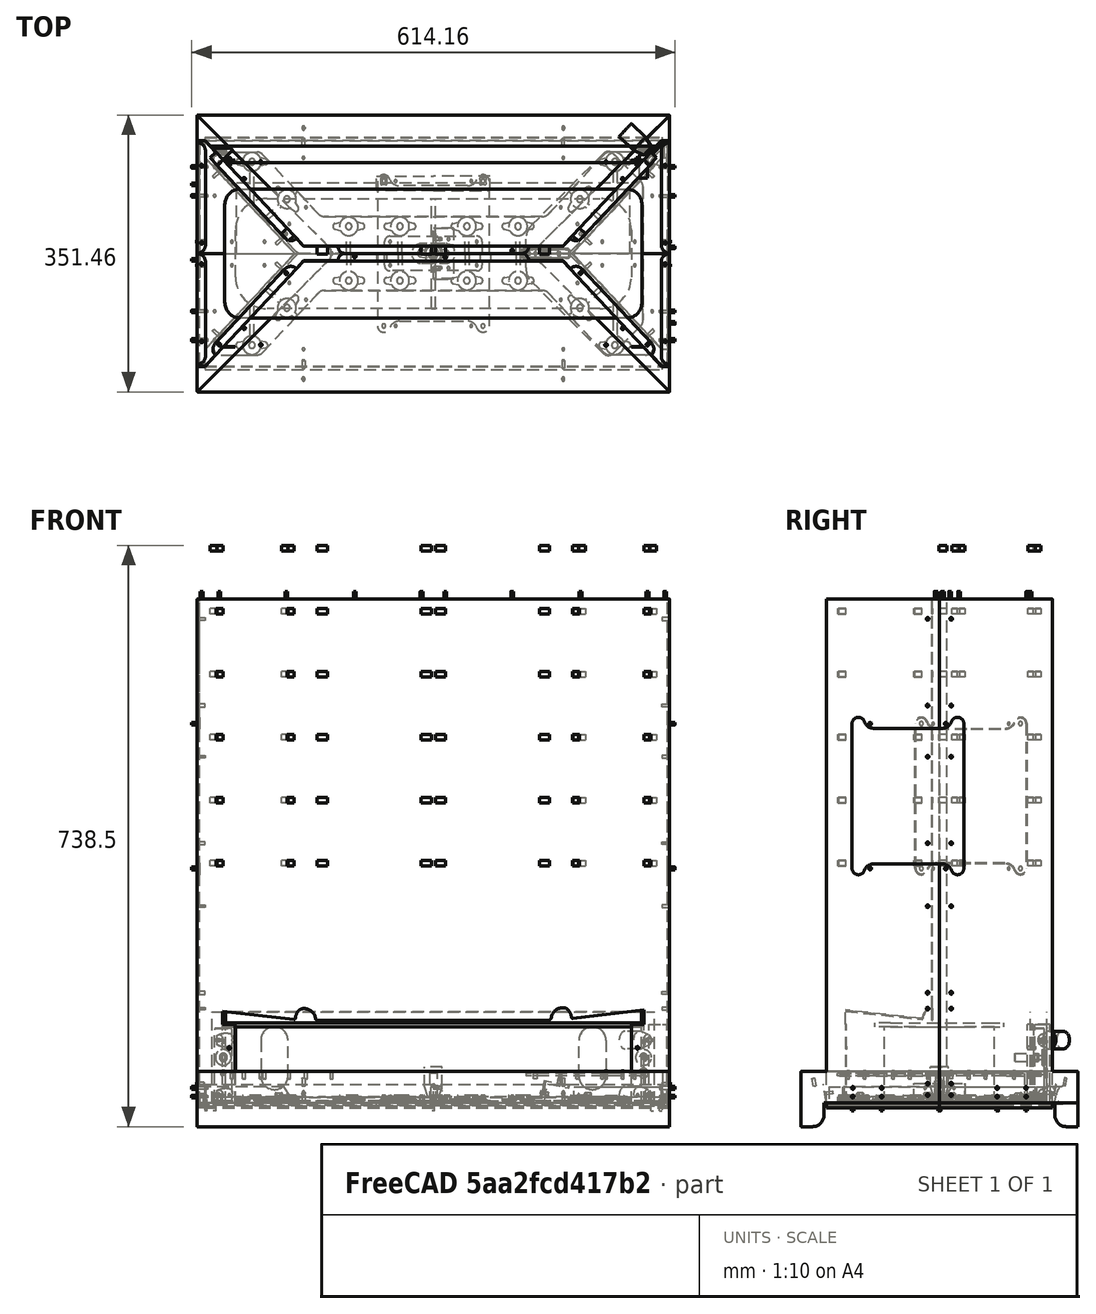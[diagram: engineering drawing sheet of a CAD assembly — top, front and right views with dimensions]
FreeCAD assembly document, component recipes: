
FREECAD ASSEMBLY — COMPONENT RECIPES ("composit_stand6")

This assembly document has 25 components, labeled P0..P24 below (a component is one placed body or linked part). 24 of them carry a construction recipe — the FreeCAD feature program that regenerates the part from scratch, quoted from this document or its linked companion documents; the rest are supplied as boundary geometry only. No exploded tour is included for this assembly.
COMPONENT P0 — recipe-attached ("basin", modeled in this document).
Construction recipe (the document's own serialized feature program — sketch geometry with constraints, then the solid features built on it; lengths are millimeters unless a unit is written):

FEATURE [Sketcher::SketchObject] Sketch015
  AttachmentOffset = pos=(0,0,97) rot=(0,0,1;0rad)
  FullyConstrained = true
  MapMode = 5
  Placement = pos=(0,0,97) rot=(0,0,1;0rad)
  Support = -> [XY_Plane006]
  expr: .AttachmentOffset.Base.z = Pad001.Length
  sketch-geometry (10):
    g0: ArcOfCircle CenterX=-245 CenterY=-62 CenterZ=0 NormalX=0 NormalY=0 NormalZ=1 AngleXU=0 Radius=20 StartAngle=3.14159 EndAngle=4.71239
    g1: LineSegment StartX=-265 StartY=-62 StartZ=0 EndX=-265 EndY=62 EndZ=0
    g2: ArcOfCircle CenterX=-245 CenterY=62 CenterZ=0 NormalX=0 NormalY=0 NormalZ=1 AngleXU=0 Radius=20 StartAngle=1.5708 EndAngle=3.14159
    g3: LineSegment StartX=-245 StartY=82 StartZ=0 EndX=245 EndY=82 EndZ=0
    g4: ArcOfCircle CenterX=245 CenterY=62 CenterZ=0 NormalX=0 NormalY=0 NormalZ=1 AngleXU=0 Radius=20 StartAngle=8.58e-14 EndAngle=1.5708
    g5: LineSegment StartX=265 StartY=62 StartZ=0 EndX=265 EndY=-62 EndZ=0
    g6: ArcOfCircle CenterX=245 CenterY=-62 CenterZ=0 NormalX=0 NormalY=0 NormalZ=1 AngleXU=0 Radius=20 StartAngle=4.71239 EndAngle=6.28319
    g7: LineSegment StartX=245 StartY=-82 StartZ=0 EndX=-245 EndY=-82 EndZ=0
    g8: GeomPoint X=-265 Y=-82 Z=0
    g9: GeomPoint X=265 Y=82 Z=0
  constraints (23):
    c: Tangent(g0,g1) = 1.5708
    c: Tangent(g1,g2) = 1.5708
    c: Tangent(g2,g3) = 1.5708
    c: Tangent(g3,g4) = 1.5708
    c: Tangent(g4,g5) = 1.5708
    c: Tangent(g5,g6) = 1.5708
    c: Tangent(g6,g7) = 1.5708
    c: Tangent(g7,g0) = 1.5708
    c: Horizontal(g3)
    c: Horizontal(g7)
    c: Vertical(g1)
    c: Vertical(g5)
    c: Equal(g0,g2)
    c: Equal(g2,g4)
    c: Equal(g4,g6)
    c: PointOnObject(g8,g1)
    c: PointOnObject(g8,g7)
    c: PointOnObject(g9,g3)
    c: PointOnObject(g9,g5)
    c: Symmetric(g8,g9,g-1)
    c: DistanceX(g8,g9) = 530
    c: DistanceY(g8,g9) = 164
    c: Radius(g4) = 20
FEATURE [Sketcher::SketchObject] Sketch016
  FullyConstrained = true
  MapMode = 5
  Support = -> [XY_Plane006]
  sketch-geometry (10):
    g0: ArcOfCircle CenterX=-211.5 CenterY=-30 CenterZ=0 NormalX=0 NormalY=0 NormalZ=1 AngleXU=0 Radius=40 StartAngle=3.14159 EndAngle=4.71239
    g1: LineSegment StartX=-251.5 StartY=-30 StartZ=0 EndX=-251.5 EndY=30 EndZ=0
    g2: ArcOfCircle CenterX=-211.5 CenterY=30 CenterZ=0 NormalX=0 NormalY=0 NormalZ=1 AngleXU=0 Radius=40 StartAngle=1.5708 EndAngle=3.14159
    g3: LineSegment StartX=-211.5 StartY=70 StartZ=0 EndX=211.5 EndY=70 EndZ=0
    g4: ArcOfCircle CenterX=211.5 CenterY=30 CenterZ=0 NormalX=0 NormalY=0 NormalZ=1 AngleXU=0 Radius=40 StartAngle=6.3434e-12 EndAngle=1.5708
    g5: LineSegment StartX=251.5 StartY=30 StartZ=0 EndX=251.5 EndY=-30 EndZ=0
    g6: ArcOfCircle CenterX=211.5 CenterY=-30 CenterZ=0 NormalX=0 NormalY=0 NormalZ=1 AngleXU=0 Radius=40 StartAngle=4.71239 EndAngle=6.28319
    g7: LineSegment StartX=211.5 StartY=-70 StartZ=0 EndX=-211.5 EndY=-70 EndZ=0
    g8: GeomPoint X=-251.5 Y=-70 Z=0
    g9: GeomPoint X=251.5 Y=70 Z=0
  constraints (23):
    c: Tangent(g0,g1) = 1.5708
    c: Tangent(g1,g2) = 1.5708
    c: Tangent(g2,g3) = 1.5708
    c: Tangent(g3,g4) = 1.5708
    c: Tangent(g4,g5) = 1.5708
    c: Tangent(g5,g6) = 1.5708
    c: Tangent(g6,g7) = 1.5708
    c: Tangent(g7,g0) = 1.5708
    c: Horizontal(g3)
    c: Horizontal(g7)
    c: Vertical(g1)
    c: Vertical(g5)
    c: Equal(g0,g2)
    c: Equal(g2,g4)
    c: Equal(g4,g6)
    c: PointOnObject(g8,g1)
    c: PointOnObject(g8,g7)
    c: PointOnObject(g9,g3)
    c: PointOnObject(g9,g5)
    c: Symmetric(g8,g9,g-1)
    c: Radius(g4) = 40
    c: DistanceX(g8,g9) = 503
    c: DistanceY(g8,g9) = 140
FEATURE [PartDesign::Pad] Pad001
  Direction = (0,0,1)
  Length = 97
  Length2 = 10
  Profile = -> Sketch016
  ReferenceAxis = -> Sketch016 [N_Axis]
  Type = 0
FEATURE [PartDesign::Pad] Pad002
  BaseFeature = -> Pad001
  Direction = (0,0,1)
  Length = 5
  Length2 = 10
  Profile = -> Sketch015
  ReferenceAxis = -> Sketch015 [N_Axis]
  Type = 0
FEATURE [PartDesign::Body] Body005  label="basin"
  Group = -> [Sketch015,Sketch016,Pad001,Pad002]
  Origin = -> Origin006
  Tip = -> Pad002
COMPONENT P1 — recipe-attached ("face2_material_0.30ansi", modeled in this document).
Construction recipe (the document's own serialized feature program — sketch geometry with constraints, then the solid features built on it; lengths are millimeters unless a unit is written):

FEATURE [PartDesign::FeatureBase] BaseFeature
  BaseFeature = -> Boolean
  expr: BaseFeature = <<face2_origin>>._self
FEATURE [PartDesign::Boolean] Boolean001
  BaseFeature = -> BaseFeature
  Group = -> [Compound009]
  Type = 1
FEATURE [PartDesign::Boolean] Boolean017
  BaseFeature = -> Boolean001
  Group = -> [Compound025]
  Type = 0
FEATURE [PartDesign::Body] Body007  label="face2_material_0.30ansi"
  BaseFeature = -> Boolean
  Group = -> [BaseFeature,Boolean001,Boolean017]
  Origin = -> Origin008
  Placement = pos=(0,0,0) rot=(0,0,1;3.14159rad)
  Tip = -> Boolean017
COMPONENT P2 — recipe-attached ("electric_shield", modeled in this document).
Construction recipe (the document's own serialized feature program — sketch geometry with constraints, then the solid features built on it; lengths are millimeters unless a unit is written):

FEATURE [PartDesign::SubShapeBinder] Binder045
  BindCopyOnChange = 0
  BindMode = 0
  ClaimChildren = true
  Context = -> Body008 [Binder045.]
  Fuse = false
  MakeFace = true
  OffsetFill = false
  OffsetIntersection = false
  OffsetJoinType = 0
  OffsetOpenResult = false
  PartialLoad = false
  Relative = false
  Support = -> [Connect005]
  _Version = 2
  expr: Support = <<Connect005>>._self
FEATURE [PartDesign::Pad] Pad015
  Direction = (0,0,1)
  Length = 0.3
  Length2 = 10
  Profile = -> Binder045
  Type = 0
FEATURE [PartDesign::Boolean] Boolean002
  BaseFeature = -> Pad015
  Group = -> [Compound010]
  Type = 1
FEATURE [PartDesign::Body] Body008  label="electric_shield"
  Group = -> [Binder045,Pad015,Boolean002]
  Origin = -> Origin009
  Placement = pos=(-297.084,40,390) rot=(0.57735,-0.57735,-0.57735;2.0944rad)
  Tip = -> Boolean002
  expr: Placement = <<electric_shield_placement>>.Placement
COMPONENT P3 — recipe-attached ("lamp_fix", modeled in this document).
Construction recipe (the document's own serialized feature program — sketch geometry with constraints, then the solid features built on it; lengths are millimeters unless a unit is written):

FEATURE [PartDesign::SubShapeBinder] Binder022
  BindCopyOnChange = 0
  BindMode = 0
  ClaimChildren = true
  Context = -> Body012 [Binder022.]
  Fuse = false
  MakeFace = true
  OffsetFill = false
  OffsetIntersection = false
  OffsetJoinType = 0
  OffsetOpenResult = false
  PartialLoad = false
  Placement = pos=(0,0,0) rot=(1,0,0;1.5708rad)
  Relative = false
  Support = -> [Sketch031]
  _Version = 2
FEATURE [PartDesign::Pad] Pad007
  Direction = (0,-1,2e-16)
  Length = 10
  Length2 = 10
  Midplane = true
  Placement = pos=(0,0,0) rot=(1,0,0;1.5708rad)
  Profile = -> Binder022
  Type = 0
FEATURE [PartDesign::Boolean] Boolean009
  BaseFeature = -> Pad007
  Group = -> [Compound018]
  Type = 1
FEATURE [PartDesign::Body] Body012  label="lamp_fix"
  Group = -> [Binder022,Pad007,Boolean009]
  Origin = -> Origin014
  Tip = -> Boolean009
COMPONENT P4 — recipe-attached ("faces_connect", modeled in this document).
Construction recipe (the document's own serialized feature program — sketch geometry with constraints, then the solid features built on it; lengths are millimeters unless a unit is written):

FEATURE [PartDesign::SubShapeBinder] Binder023
  BindCopyOnChange = 0
  BindMode = 0
  ClaimChildren = true
  Context = -> Body013 [Binder023.]
  Fuse = false
  MakeFace = true
  OffsetFill = false
  OffsetIntersection = false
  OffsetJoinType = 0
  OffsetOpenResult = false
  PartialLoad = false
  Relative = false
  Support = -> [Sketch032]
  _Version = 2
FEATURE [PartDesign::Pad] Pad008
  Direction = (0,0,1)
  Length = 3
  Length2 = 10
  Profile = -> Binder023
  Type = 0
FEATURE [PartDesign::Boolean] Boolean010
  BaseFeature = -> Pad008
  Group = -> [Populate027]
  Type = 1
FEATURE [PartDesign::Body] Body013  label="faces_connect"
  Group = -> [Binder023,Pad008,Boolean010]
  Origin = -> Origin015
  Tip = -> Boolean010
COMPONENT P5 — recipe-attached ("electric_shield_jamb", modeled in this document).
Construction recipe (the document's own serialized feature program — sketch geometry with constraints, then the solid features built on it; lengths are millimeters unless a unit is written):

FEATURE [PartDesign::SubShapeBinder] Binder025
  BindCopyOnChange = 0
  BindMode = 0
  ClaimChildren = true
  Context = -> Body015 [Binder025.]
  Fuse = false
  MakeFace = true
  OffsetFill = false
  OffsetIntersection = false
  OffsetJoinType = 0
  OffsetOpenResult = false
  PartialLoad = false
  Relative = false
  Support = -> [Compound021]
  _Version = 2
FEATURE [PartDesign::Pad] Pad009
  Direction = (0,0,1)
  Length = 3
  Length2 = 10
  Profile = -> Binder025
  Type = 0
FEATURE [PartDesign::Boolean] Boolean013
  BaseFeature = -> Pad009
  Group = -> [Fusion003]
  Type = 1
FEATURE [PartDesign::Body] Body015  label="electric_shield_jamb"
  Group = -> [Binder025,Pad009,Boolean013]
  Origin = -> Origin017
  Tip = -> Boolean013
COMPONENT P6 — recipe-attached ("screw_pocket", modeled in this document).
Construction recipe (the document's own serialized feature program — sketch geometry with constraints, then the solid features built on it; lengths are millimeters unless a unit is written):

FEATURE [Sketcher::SketchObject] Sketch040
  FullyConstrained = true
  MapMode = 5
  Support = -> [XY_Plane018]
  sketch-geometry (7):
    g0: ArcOfCircle CenterX=2.79363 CenterY=2.79363 CenterZ=0 NormalX=0 NormalY=0 NormalZ=1 AngleXU=0 Radius=1.6 StartAngle=5.49779 EndAngle=8.63938
    g1: LineSegment StartX=3.925 StartY=3.925 StartZ=0 EndX=1.66226 EndY=3.925 EndZ=0
    g2: LineSegment StartX=1.66226 StartY=3.925 StartZ=0 EndX=0 EndY=3.925 EndZ=0
    g3: LineSegment StartX=3.925 StartY=0 StartZ=0 EndX=3.925 EndY=1.66226 EndZ=0
    g4: LineSegment StartX=3.925 StartY=1.66226 StartZ=0 EndX=3.925 EndY=3.925 EndZ=0
    g5: LineSegment StartX=0 StartY=3.925 StartZ=0 EndX=0 EndY=0 EndZ=0
    g6: LineSegment StartX=0 StartY=0 StartZ=0 EndX=3.925 EndY=0 EndZ=0
  constraints (20):
    c: PointOnObject(g3,g-1)
    c: Coincident(g4,g1)
    c: PointOnObject(g2,g-2)
    c: Coincident(g1,g2)
    c: Horizontal(g1)
    c: Horizontal(g2)
    c: Coincident(g3,g4)
    c: Vertical(g3)
    c: Vertical(g4)
    c: Coincident(g2,g0)
    c: Coincident(g3,g0)
    c: Coincident(g2,g5)
    c: Coincident(g5,g-1)
    c: Coincident(g5,g6)
    c: Coincident(g6,g3)
    c: Equal(g6,g5)
    c: DistanceX(g6,g6) = 3.925
    c: PointOnObject(g1,g0)
    c: Equal(g4,g1)
    c: Diameter(g0) = 3.2
FEATURE [PartDesign::Pad] Pad010
  Direction = (0,0,1)
  Length = 3
  Length2 = 10
  Midplane = true
  Profile = -> Sketch040
  ReferenceAxis = -> Sketch040 [N_Axis]
  Type = 0
FEATURE [PartDesign::PolarPattern] PolarPattern001
  Angle = 360
  Axis = -> Sketch040 [N_Axis]
  BaseFeature = -> Pad010
  Mode = 0
  Occurrences = 4
  Offset = 120
  Originals = -> [Pad010]
  Refine = true
FEATURE [PartDesign::Body] Body016  label="screw_pocket"
  Group = -> [Sketch040,Pad010,PolarPattern001]
  Origin = -> Origin018
  Tip = -> PolarPattern001
COMPONENT P7 — recipe-attached ("front_shield_jamb", modeled in this document).
Construction recipe (the document's own serialized feature program — sketch geometry with constraints, then the solid features built on it; lengths are millimeters unless a unit is written):

FEATURE [PartDesign::SubShapeBinder] Binder030
  BindCopyOnChange = 0
  BindMode = 0
  ClaimChildren = false
  Context = -> Body018 [Binder030.]
  Fuse = false
  MakeFace = true
  OffsetFill = false
  OffsetIntersection = false
  OffsetJoinType = 0
  OffsetOpenResult = false
  PartialLoad = false
  Relative = true
  Support = -> [Sketch001]
  _Version = 2
FEATURE [PartDesign::CoordinateSystem] Local_CS001
  AttacherType = Attacher::AttachEngine3D
  MapMode = 1
  Placement = pos=(266.917,133.558,0) rot=(0,0.707107,0.707107;3.14159rad)
FEATURE [PartDesign::SubShapeBinder] Binder039
  BindCopyOnChange = 0
  BindMode = 0
  ClaimChildren = true
  Context = -> Body018 [Binder039.]
  Fuse = false
  MakeFace = true
  OffsetFill = false
  OffsetIntersection = false
  OffsetJoinType = 0
  OffsetOpenResult = false
  PartialLoad = false
  Relative = false
  Support = -> [Sketch056]
  _Version = 2
FEATURE [PartDesign::Pad] Pad011
  Direction = (0,0,1)
  Length = 95
  Length2 = 10
  Profile = -> Binder039
  Type = 0
FEATURE [PartDesign::Fillet] Fillet
  Base = -> Pad011
  BaseFeature = -> Pad011
  Radius = 2
  SupportTransform = false
  UseAllEdges = true
FEATURE [PartDesign::Boolean] Boolean016
  BaseFeature = -> Fillet
  Group = -> [Fusion004]
  Type = 1
FEATURE [PartDesign::Body] Body018  label="front_shield_jamb"
  Group = -> [Binder030,Pad011,Local_CS001,Binder039,Fillet,Boolean016]
  Origin = -> Origin025
  Tip = -> Boolean016
COMPONENT P8 — recipe-attached ("Body019", modeled in this document).
Construction recipe (the document's own serialized feature program — sketch geometry with constraints, then the solid features built on it; lengths are millimeters unless a unit is written):

FEATURE [PartDesign::SubShapeBinder] Binder032
  BindCopyOnChange = 0
  BindMode = 0
  ClaimChildren = true
  Context = -> Body019 [Binder032.]
  Fuse = false
  MakeFace = true
  OffsetFill = false
  OffsetIntersection = false
  OffsetJoinType = 0
  OffsetOpenResult = false
  PartialLoad = false
  Relative = false
  Support = -> [Connect002]
  _Version = 2
FEATURE [PartDesign::FeaturePython] BaseBend006  # WARN: FeaturePython — macro-defined, semantics opaque (R4)
  BendSide = 1
  BendSketch = -> Binder032
  MidPlane = false
  Reverse = false
  length = 116
  radius = 0.1
  thickness = 0.3
FEATURE [PartDesign::Boolean] Boolean020
  BaseFeature = -> BaseBend006
  Group = -> [Compound028]
  Refine = true
  Type = 1
FEATURE [PartDesign::Body] Body019
  Group = -> [Binder032,BaseBend006,Boolean020]
  Origin = -> Origin026
  Tip = -> Boolean020
COMPONENT P9 — recipe-attached ("Body020", modeled in this document).
Construction recipe (the document's own serialized feature program — sketch geometry with constraints, then the solid features built on it; lengths are millimeters unless a unit is written):

FEATURE [PartDesign::SubShapeBinder] Binder033
  BindCopyOnChange = 0
  BindMode = 0
  ClaimChildren = true
  Context = -> Body020 [Binder033.]
  Fuse = false
  MakeFace = true
  OffsetFill = false
  OffsetIntersection = false
  OffsetJoinType = 0
  OffsetOpenResult = false
  PartialLoad = false
  Relative = false
  Support = -> [Sketch051]
  _Version = 2
FEATURE [PartDesign::FeaturePython] BaseBend007  # WARN: FeaturePython — macro-defined, semantics opaque (R4)
  BendSide = 0
  BendSketch = -> Binder033
  MidPlane = false
  Reverse = false
  length = 100
  radius = 0.1
  thickness = 0.3
FEATURE [PartDesign::Boolean] Boolean018
  BaseFeature = -> BaseBend007
  Group = -> [Compound026]
  Type = 1
FEATURE [PartDesign::Body] Body020
  Group = -> [Binder033,BaseBend007,Boolean018]
  Origin = -> Origin027
  Tip = -> Boolean018
COMPONENT P10 — recipe-attached ("Body021", modeled in this document).
Construction recipe (the document's own serialized feature program — sketch geometry with constraints, then the solid features built on it; lengths are millimeters unless a unit is written):

FEATURE [PartDesign::SubShapeBinder] Binder034
  BindCopyOnChange = 0
  BindMode = 0
  ClaimChildren = true
  Context = -> Body021 [Binder034.]
  Fuse = false
  MakeFace = true
  OffsetFill = false
  OffsetIntersection = false
  OffsetJoinType = 0
  OffsetOpenResult = false
  PartialLoad = false
  Relative = false
  Support = -> [Part__Mirroring009]
  _Version = 2
FEATURE [PartDesign::FeaturePython] BaseBend008  # WARN: FeaturePython — macro-defined, semantics opaque (R4)
  BendSide = 1
  BendSketch = -> Binder034
  MidPlane = false
  Reverse = false
  length = 100
  radius = 0.1
  thickness = 0.3
FEATURE [PartDesign::Boolean] Boolean019
  BaseFeature = -> BaseBend008
  Group = -> [Compound027]
  Type = 1
FEATURE [PartDesign::Body] Body021
  Group = -> [Binder034,BaseBend008,Boolean019]
  Origin = -> Origin028
  Tip = -> Boolean019
COMPONENT P11 — recipe-attached ("Body022", modeled in this document).
Construction recipe (the document's own serialized feature program — sketch geometry with constraints, then the solid features built on it; lengths are millimeters unless a unit is written):

FEATURE [PartDesign::SubShapeBinder] Binder035
  BindCopyOnChange = 0
  BindMode = 0
  ClaimChildren = true
  Context = -> Part002 [Part004.Body017.Boolean015.Body022.Binder035.]
  Fuse = false
  MakeFace = true
  OffsetFill = false
  OffsetIntersection = false
  OffsetJoinType = 0
  OffsetOpenResult = false
  PartialLoad = false
  Relative = true
  Support = -> [Compound023]
  _Version = 2
  expr: Support = <<Compound023>>._self
FEATURE [PartDesign::FeaturePython] BaseBend009  # WARN: FeaturePython — macro-defined, semantics opaque (R4)
  BendSide = 0
  BendSketch = -> Binder035
  MidPlane = false
  Reverse = true
  length = 30
  radius = 0.1
  thickness = 0.3
FEATURE [Sketcher::SketchObject] Sketch052
  ExternalGeometry = -> [Binder035]
  FullyConstrained = true
  MapMode = 5
  Placement = pos=(0,0,0) rot=(0.57735,0.57735,0.57735;2.0944rad)
  Support = -> [YZ_Plane029]
  sketch-geometry (3):
    g0: ArcOfCircle CenterX=161.558 CenterY=-15 CenterZ=0 NormalX=0 NormalY=0 NormalZ=1 AngleXU=0 Radius=15 StartAngle=3.14159 EndAngle=4.71239
    g1: LineSegment StartX=146.558 StartY=-15 StartZ=0 EndX=146.558 EndY=-30 EndZ=0
    g2: LineSegment StartX=146.558 StartY=-30 StartZ=0 EndX=161.558 EndY=-30 EndZ=0
  constraints (9):
    c: Coincident(g1,g2)
    c: Coincident(g2,g0)
    c: Tangent(g2,g0)
    c: Tangent(g0,g1) = -1.5708
    c: Horizontal(g2)
    c: Vertical(g1)
    c: Vertical(g1,g-3)
    c: DistanceY(g1,g-3) = 30
    c: Diameter(g0) = 30
FEATURE [PartDesign::Pocket] Pocket012
  BaseFeature = -> BaseBend009
  Direction = (-1,0,0)
  Length = 5
  Length2 = 5
  Midplane = true
  Profile = -> Sketch052
  ReferenceAxis = -> Sketch052 [N_Axis]
  Type = 1
FEATURE [PartDesign::Body] Body022
  Group = -> [Binder035,BaseBend009,Sketch052,Pocket012]
  Origin = -> Origin029
  Tip = -> Pocket012
COMPONENT P12 — recipe-attached ("Body024", modeled in this document).
Construction recipe (the document's own serialized feature program — sketch geometry with constraints, then the solid features built on it; lengths are millimeters unless a unit is written):

FEATURE [PartDesign::SubShapeBinder] Binder036
  BindCopyOnChange = 0
  BindMode = 0
  ClaimChildren = true
  Context = -> Body024 [Binder036.]
  Fuse = false
  MakeFace = true
  OffsetFill = false
  OffsetIntersection = false
  OffsetJoinType = 0
  OffsetOpenResult = false
  PartialLoad = false
  Relative = false
  Support = -> [Connect003]
  _Version = 2
FEATURE [PartDesign::Pad] Pad012
  Direction = (0,0,1)
  Length = 3
  Length2 = 10
  Profile = -> Binder036
  Refine = true
  Type = 0
FEATURE [PartDesign::Boolean] Boolean021
  BaseFeature = -> Pad012
  Group = -> [Compound031]
  Type = 1
FEATURE [PartDesign::Body] Body024
  Group = -> [Binder036,Pad012,Boolean021]
  Origin = -> Origin031
  Tip = -> Boolean021
COMPONENT P13 — recipe-attached ("Body025", modeled in this document).
Construction recipe (the document's own serialized feature program — sketch geometry with constraints, then the solid features built on it; lengths are millimeters unless a unit is written):

FEATURE [Sketcher::SketchObject] Sketch055
  FullyConstrained = true
  MapMode = 5
  Placement = pos=(0,0,0) rot=(1,0,0;1.5708rad)
  Support = -> [XZ_Plane032]
  sketch-geometry (7):
    g0: LineSegment StartX=0 StartY=0 StartZ=0 EndX=7 EndY=0 EndZ=0
    g1: LineSegment StartX=7 StartY=0 StartZ=0 EndX=11.25 EndY=14 EndZ=0
    g2: LineSegment StartX=11.25 StartY=14 StartZ=0 EndX=0 EndY=14 EndZ=0
    g3: LineSegment StartX=0 StartY=14 StartZ=0 EndX=0 EndY=0 EndZ=0
    g4: LineSegment StartX=11.25 StartY=14 StartZ=0 EndX=11.25 EndY=39 EndZ=0
    g5: LineSegment StartX=11.25 StartY=39 StartZ=0 EndX=0 EndY=39 EndZ=0
    g6: LineSegment StartX=0 StartY=39 StartZ=0 EndX=0 EndY=14 EndZ=0
  constraints (19):
    c: Horizontal(g0)
    c: Coincident(g0,g1)
    c: Coincident(g1,g2)
    c: Horizontal(g2)
    c: Coincident(g2,g3)
    c: Coincident(g3,g0)
    c: Vertical(g3)
    c: Coincident(g0,g-1)
    c: DistanceX(g2,g2) = 11.25
    c: DistanceX(g0,g0) = 7
    c: DistanceY(g3,g3) = 14
    c: Coincident(g1,g4)
    c: Vertical(g4)
    c: Coincident(g4,g5)
    c: Horizontal(g5)
    c: Coincident(g5,g6)
    c: Coincident(g6,g3)
    c: Vertical(g6)
    c: DistanceY(g6,g6) = 25
FEATURE [PartDesign::Revolution] Revolution
  Angle = 360
  Axis = (0,2e-16,1)
  Base = (0,0,0)
  Placement = pos=(0,0,0) rot=(1,0,0;1.5708rad)
  Profile = -> Sketch055
  ReferenceAxis = -> Sketch055 [V_Axis]
  Reversed = true
FEATURE [PartDesign::Body] Body025
  Group = -> [Sketch055,Revolution]
  Origin = -> Origin032
  Placement = pos=(0,0,7) rot=(0,0,1;0rad)
  Tip = -> Revolution
COMPONENT P14 — recipe-attached ("magnet", modeled in this document).
Construction recipe (the document's own serialized feature program — sketch geometry with constraints, then the solid features built on it; lengths are millimeters unless a unit is written):

FEATURE [Sketcher::SketchObject] Sketch057
  FullyConstrained = true
  MapMode = 5
  Support = -> [XY_Plane033]
  sketch-geometry (1):
    g0: Circle CenterX=0 CenterY=0 CenterZ=0 NormalX=0 NormalY=0 NormalZ=1 AngleXU=0 Radius=10
  constraints (2):
    c: Coincident(g0,g-1)
    c: Diameter(g0) = 20
FEATURE [PartDesign::Pad] Pad013  label="magnet_pad"
  Direction = (0,0,1)
  Length = 3
  Length2 = 10
  Profile = -> Sketch057
  ReferenceAxis = -> Sketch057 [N_Axis]
  Type = 0
FEATURE [PartDesign::Body] Body026  label="magnet"
  Group = -> [Sketch057,Pad013]
  Origin = -> Origin033
  Tip = -> Pad013
COMPONENT P15 — recipe-attached ("front_shield", modeled in this document).
Construction recipe (the document's own serialized feature program — sketch geometry with constraints, then the solid features built on it; lengths are millimeters unless a unit is written):

FEATURE [PartDesign::SubShapeBinder] Binder040
  BindCopyOnChange = 0
  BindMode = 0
  ClaimChildren = true
  Context = -> Body027 [Binder040.]
  Fuse = false
  MakeFace = true
  OffsetFill = false
  OffsetIntersection = false
  OffsetJoinType = 0
  OffsetOpenResult = false
  PartialLoad = false
  Relative = false
  Support = -> [Connect004]
  _Version = 2
FEATURE [PartDesign::FeaturePython] BaseBend010  # WARN: FeaturePython — macro-defined, semantics opaque (R4)
  BendSide = 0
  BendSketch = -> Binder040
  MidPlane = false
  Reverse = false
  length = 116
  radius = 0.1
  thickness = 0.3
FEATURE [PartDesign::SubShapeBinder] Binder041
  BindCopyOnChange = 0
  BindMode = 0
  ClaimChildren = false
  Context = -> Body027 [Binder041.]
  Fuse = false
  MakeFace = true
  OffsetFill = false
  OffsetIntersection = false
  OffsetJoinType = 0
  OffsetOpenResult = false
  PartialLoad = false
  Placement = pos=(202,0,57) rot=(0.57735,0.57735,-0.57735;2.0944rad)
  Relative = true
  Support = -> [<external embedded_hand_34x80.FCStd>#Cut]
  _Version = 2
FEATURE [PartDesign::Pocket] Pocket013
  BaseFeature = -> BaseBend010
  Direction = (0,1,0)
  Length = 5
  Length2 = 5
  Profile = -> Binder041
  Type = 1
FEATURE [PartDesign::Mirrored] Mirrored010
  BaseFeature = -> Pocket013
  MirrorPlane = -> YZ_Plane034
  Originals = -> [Pocket013]
FEATURE [PartDesign::Boolean] Boolean022
  BaseFeature = -> Mirrored010
  Group = -> [Compound032]
  Refine = true
  Type = 1
FEATURE [PartDesign::Body] Body027  label="front_shield"
  Group = -> [Binder040,BaseBend010,Binder041,Pocket013,Mirrored010,Boolean022]
  Origin = -> Origin034
  Tip = -> Boolean022
COMPONENT P16 — recipe-attached ("lamp_holder", modeled in this document).
Construction recipe (the document's own serialized feature program — sketch geometry with constraints, then the solid features built on it; lengths are millimeters unless a unit is written):

FEATURE [PartDesign::SubShapeBinder] Binder042
  BindCopyOnChange = 0
  BindMode = 0
  ClaimChildren = true
  Context = -> Part [Body028.Binder042.]
  Fuse = false
  MakeFace = true
  OffsetFill = false
  OffsetIntersection = false
  OffsetJoinType = 0
  OffsetOpenResult = false
  PartialLoad = false
  Relative = true
  Support = -> [Sketch012]
  _Version = 2
  expr: Support = <<top_base_sketch>>._self
FEATURE [PartDesign::SubShapeBinder] Binder043
  BindCopyOnChange = 0
  BindMode = 0
  ClaimChildren = true
  Context = -> Part [Body028.Binder043.]
  Fuse = false
  MakeFace = true
  OffsetFill = false
  OffsetIntersection = false
  OffsetJoinType = 0
  OffsetOpenResult = false
  PartialLoad = false
  Relative = true
  Support = -> [Sketch030]
  _Version = 2
FEATURE [Sketcher::SketchObject] Sketch059
  ExternalGeometry = -> [Binder042,Binder043]
  FullyConstrained = true
  MapMode = 5
  Support = -> [XY_Plane035]
  sketch-geometry (14):
    g0: LineSegment StartX=113.536 StartY=3 StartZ=0 EndX=141.041 EndY=3 EndZ=0
    g1: LineSegment StartX=141.041 StartY=3 StartZ=0 EndX=144.771 EndY=24.1563 EndZ=0
    g2: LineSegment StartX=144.771 StartY=24.1563 StartZ=0 EndX=171.35 EndY=19.4697 EndZ=0
    g3: LineSegment StartX=171.35 StartY=19.4697 StartZ=0 EndX=171.871 EndY=22.4241 EndZ=0
    g4: LineSegment StartX=171.871 StartY=22.4241 StartZ=0 EndX=140.368 EndY=27.979 EndZ=0
    g5: LineSegment StartX=140.368 StartY=27.979 StartZ=0 EndX=137.574 EndY=12.1318 EndZ=0
    g6: LineSegment StartX=132.65 StartY=8 StartZ=0 EndX=113.536 EndY=8 EndZ=0
    g7: LineSegment StartX=113.536 StartY=8 StartZ=0 EndX=113.536 EndY=3 EndZ=0
    g8: LineSegment StartX=136.845 StartY=3 StartZ=0 EndX=136.845 EndY=8 EndZ=0
    g9: LineSegment StartX=136.845 StartY=8 StartZ=0 EndX=141.769 EndY=7.13176 EndZ=0
    g10: LineSegment StartX=143.995 StartY=2.47906 StartZ=0 EndX=141.041 EndY=3 EndZ=0
    g11: LineSegment StartX=141.041 StartY=3 StartZ=0 EndX=141.041 EndY=0 EndZ=0
    g12: ArcOfCircle CenterX=132.65 CenterY=13 CenterZ=0 NormalX=0 NormalY=0 NormalZ=1 AngleXU=0 Radius=5 StartAngle=4.71239 EndAngle=6.10865
    g13: GeomPoint X=136.845 Y=8 Z=0
  constraints (40):
    c: Horizontal(g0)
    c: Coincident(g0,g1)
    c: Coincident(g1,g2)
    c: Coincident(g2,g3)
    c: Coincident(g3,g4)
    c: Coincident(g4,g5)
    c: Horizontal(g6)
    c: Coincident(g6,g7)
    c: Coincident(g7,g0)
    c: Vertical(g7)
    c: PointOnObject(g8,g0)
    c: Coincident(g8,g13)
    c: Coincident(g8,g9)
    c: PointOnObject(g9,g1)
    c: Perpendicular(g2,g3)
    c: Perpendicular(g4,g3)
    c: Perpendicular(g6,g8)
    c: Perpendicular(g5,g9)
    c: Parallel(g1,g-3)
    c: Perpendicular(g2,g1)
    c: PointOnObject(g-3,g2)
    c: PointOnObject(g10,g-3)
    c: Coincident(g10,g0)
    c: Coincident(g10,g11)
    c: PointOnObject(g11,g-1)
    c: Perpendicular(g0,g11)
    c: Perpendicular(g1,g10)
    c: Equal(g11,g10)
    c: Distance(g11) = 3
    c: PointOnObject(g13,g5)
    c: PointOnObject(g13,g6)
    c: Tangent(g5,g12) = 1.5708
    c: Tangent(g6,g12) = 1.5708
    c: Radius(g12) = 5
    c: Equal(g9,g8)
    c: Parallel(g1,g5)
    c: Distance(g9) = 5
    c: Distance(g3) = 3
    c: DistanceX(g0,g-4) = 8
    c: DistanceX(g1,g3) = 27.1
FEATURE [PartDesign::SubShapeBinder] Binder044
  BindCopyOnChange = 0
  BindMode = 0
  ClaimChildren = false
  Context = -> Part [Body028.Binder044.]
  Fuse = false
  MakeFace = true
  OffsetFill = false
  OffsetIntersection = false
  OffsetJoinType = 0
  OffsetOpenResult = false
  PartialLoad = false
  Placement = pos=(0,0,0) rot=(1,0,0;1.5708rad)
  Relative = true
  Support = -> [Sketch059]
  _Version = 2
FEATURE [PartDesign::Pad] Pad014
  Direction = (0,-1,2e-16)
  Length = 12
  Length2 = 10
  Midplane = true
  Placement = pos=(0,0,0) rot=(1,0,0;1.5708rad)
  Profile = -> Binder044
  Type = 0
FEATURE [PartDesign::Boolean] Boolean023
  BaseFeature = -> Pad014
  Group = -> [Fusion006]
  Type = 1
FEATURE [PartDesign::Body] Body028  label="lamp_holder"
  Group = -> [Binder042,Sketch059,Binder043,Binder044,Pad014,Boolean023]
  Origin = -> Origin035
  Tip = -> Boolean023
COMPONENT P17 — recipe-attached ("face_to_bottom", modeled in this document).
Construction recipe (the document's own serialized feature program — sketch geometry with constraints, then the solid features built on it; lengths are millimeters unless a unit is written):

FEATURE [Sketcher::SketchObject] Sketch060
  FullyConstrained = false
  MapMode = 5
  Support = -> [XY_Plane036]
  sketch-geometry (3):
    g0: LineSegment StartX=28.5181 StartY=-32.4357 StartZ=0 EndX=0 EndY=-32.4357 EndZ=0
    g1: LineSegment StartX=0 StartY=-32.4357 StartZ=0 EndX=0 EndY=32.4357 EndZ=0
    g2: LineSegment StartX=0 StartY=32.4357 StartZ=0 EndX=28.5181 EndY=32.4357 EndZ=0
  constraints (7):
    c: PointOnObject(g0,g-2)
    c: Horizontal(g0)
    c: Coincident(g1,g0)
    c: PointOnObject(g1,g-2)
    c: Coincident(g2,g1)
    c: Horizontal(g2)
    c: Symmetric(g0,g2,g-1)
FEATURE [PartDesign::FeaturePython] BaseBend011  # WARN: FeaturePython — macro-defined, semantics opaque (R4)
  BendSide = 0
  BendSketch = -> Sketch060
  MidPlane = false
  Reverse = false
  length = 25
  radius = 0.1
  thickness = 0.3
FEATURE [PartDesign::FeaturePython] Bend005  # WARN: FeaturePython — macro-defined, semantics opaque (R4)
  AutoMiter = true
  BaseFeature = -> BaseBend011
  BendType = 1
  LengthList = [22]
  LengthSpec = 1
  ReliefFactor = 0.7
  UseReliefFactor = false
  angle = 90
  baseObject = -> BaseBend011 [Edge32,Edge3]
  bendAList = [90]
  extend1 = 0
  extend2 = 0
  gap1 = 3
  gap2 = 3
  invert = false
  kfactor = 0.5
  length = 22
  maxExtendDist = 5
  minGap = 0.1
  minReliefGap = 1
  miterangle1 = 0
  miterangle2 = 0
  offset = 0
  radius = 0.1
  reliefType = 0
  reliefd = 1
  reliefw = 0.8
  sketchflip = false
  sketchinvert = false
  unfold = false
  expr: radius = BaseBend011.radius
FEATURE [Sketcher::SketchObject] Sketch061
  ExternalGeometry = -> [Sketch060]
  FullyConstrained = true
  MapMode = 5
  Placement = pos=(0,0,0) rot=(1,0,0;1.5708rad)
  Support = -> [XZ_Plane036]
  expr: Constraints[11] = BaseBend011.length
  sketch-geometry (5):
    g0: LineSegment StartX=28.5181 StartY=7.1e-15 StartZ=0 EndX=25.5181 EndY=7.1e-15 EndZ=0
    g1: LineSegment StartX=25.5181 StartY=7.1e-15 StartZ=0 EndX=25.5181 EndY=3 EndZ=0
    g2: LineSegment StartX=25.5181 StartY=3 StartZ=0 EndX=0.4 EndY=25 EndZ=0
    g3: LineSegment StartX=0.4 StartY=25 StartZ=0 EndX=28.5181 EndY=25 EndZ=0
    g4: LineSegment StartX=28.5181 StartY=25 StartZ=0 EndX=28.5181 EndY=7.1e-15 EndZ=0
  constraints (14):
    c: Coincident(g-3,g0)
    c: Horizontal(g0)
    c: Coincident(g0,g1)
    c: Vertical(g1)
    c: Coincident(g1,g2)
    c: Coincident(g2,g3)
    c: Horizontal(g3)
    c: Coincident(g3,g4)
    c: Vertical(g4)
    c: Equal(g0,g1)
    c: DistanceX(g0,g0) = 3
    c: DistanceY(g2) = 25
    c: Coincident(g4,g0)
    c: DistanceX(g2) = 0.4
FEATURE [PartDesign::Pocket] Pocket014
  BaseFeature = -> Bend005
  Direction = (0,1,-2e-16)
  Length = 5
  Length2 = 5
  Midplane = true
  Profile = -> Sketch061
  ReferenceAxis = -> Sketch061 [N_Axis]
  Type = 1
FEATURE [PartDesign::Boolean] Boolean024
  BaseFeature = -> Pocket014
  Group = -> [Compound033]
  Type = 1
FEATURE [PartDesign::Body] Body029  label="face_to_bottom"
  Group = -> [Sketch060,BaseBend011,Bend005,Sketch061,Pocket014,Boolean024]
  Origin = -> Origin036
  Tip = -> Boolean024
COMPONENT P18 — recipe-attached ("jamb_screw_cut", modeled in this document).
Construction recipe (the document's own serialized feature program — sketch geometry with constraints, then the solid features built on it; lengths are millimeters unless a unit is written):

FEATURE [Sketcher::SketchObject] Sketch062
  FullyConstrained = true
  MapMode = 5
  Placement = pos=(0,0,0) rot=(1,0,0;1.5708rad)
  Support = -> [XZ_Plane037]
  sketch-geometry (8):
    g0: LineSegment StartX=0 StartY=9 StartZ=0 EndX=0 EndY=0 EndZ=0
    g1: LineSegment StartX=0 StartY=0 StartZ=0 EndX=6 EndY=0 EndZ=0
    g2: LineSegment StartX=6 StartY=0 StartZ=0 EndX=6 EndY=2 EndZ=0
    g3: LineSegment StartX=6 StartY=2 StartZ=0 EndX=3.6 EndY=2 EndZ=0
    g4: LineSegment StartX=2.5 StartY=4 StartZ=0 EndX=2.5 EndY=9 EndZ=0
    g5: LineSegment StartX=2.5 StartY=9 StartZ=0 EndX=0 EndY=9 EndZ=0
    g6: LineSegment StartX=3.6 StartY=2 StartZ=0 EndX=3.6 EndY=4 EndZ=0
    g7: LineSegment StartX=3.6 StartY=4 StartZ=0 EndX=2.5 EndY=4 EndZ=0
  constraints (23):
    c: PointOnObject(g0,g-2)
    c: Coincident(g0,g-1)
    c: Coincident(g0,g1)
    c: PointOnObject(g1,g-1)
    c: Coincident(g1,g2)
    c: Vertical(g2)
    c: Coincident(g2,g3)
    c: Horizontal(g3)
    c: Vertical(g4)
    c: Coincident(g4,g5)
    c: Coincident(g5,g0)
    c: Horizontal(g5)
    c: DistanceX(g1,g1) = 6
    c: DistanceY(g2,g2) = 2
    c: Vertical(g6)
    c: Coincident(g7,g6)
    c: Horizontal(g7)
    c: Coincident(g3,g6)
    c: Coincident(g4,g7)
    c: DistanceX(g3) = 3.6
    c: DistanceY(g6) = 4
    c: DistanceY(g0,g0) = 9
    c: DistanceX(g4) = 2.5
FEATURE [PartDesign::Revolution] Revolution001
  Angle = 360
  Axis = (0,2e-16,1)
  Base = (0,0,0)
  Placement = pos=(0,0,0) rot=(1,0,0;1.5708rad)
  Profile = -> Sketch062
  ReferenceAxis = -> Sketch062 [V_Axis]
  Reversed = true
FEATURE [PartDesign::Body] Body030  label="jamb_screw_cut"
  Group = -> [Sketch062,Revolution001]
  Origin = -> Origin037
  Tip = -> Revolution001
COMPONENT P19 — recipe-attached ("Body031", modeled in this document).
Construction recipe (the document's own serialized feature program — sketch geometry with constraints, then the solid features built on it; lengths are millimeters unless a unit is written):

FEATURE [PartDesign::SubShapeBinder] Binder046
  BindCopyOnChange = 0
  BindMode = 0
  ClaimChildren = false
  Context = -> Body031 [Binder046.]
  Fuse = false
  MakeFace = true
  OffsetFill = false
  OffsetIntersection = false
  OffsetJoinType = 0
  OffsetOpenResult = false
  PartialLoad = false
  Relative = true
  Support = -> [Sketch063]
  _Version = 2
FEATURE [PartDesign::FeaturePython] BaseBend012  # WARN: FeaturePython — macro-defined, semantics opaque (R4)
  BendSide = 0
  BendSketch = -> Binder046
  MidPlane = false
  Reverse = false
  length = 100
  radius = 0.1
  thickness = 0.3
FEATURE [PartDesign::FeaturePython] Bend006  # WARN: FeaturePython — macro-defined, semantics opaque (R4)
  AutoMiter = true
  BaseFeature = -> BaseBend012
  BendType = 1
  LengthList = [0.1]
  LengthSpec = 0
  ReliefFactor = 0.7
  UseReliefFactor = false
  angle = 90
  baseObject = -> BaseBend012 [Edge3,Edge32]
  bendAList = [90]
  extend1 = 0
  extend2 = 0
  gap1 = 0
  gap2 = 0
  invert = false
  kfactor = 0.5
  length = 0.1
  maxExtendDist = 5
  minGap = 0.1
  minReliefGap = 1
  miterangle1 = 0
  miterangle2 = 0
  offset = 0
  radius = 0.1
  reliefType = 0
  reliefd = 1
  reliefw = 0.8
  sketchflip = false
  sketchinvert = false
  unfold = false
  expr: radius = BaseBend012.radius
FEATURE [Sketcher::SketchObject] Sketch064
  ExternalGeometry = -> [Binder046]
  FullyConstrained = false
  MapMode = 5
  Support = -> [XY_Plane038]
  sketch-geometry (18):
    g0: LineSegment StartX=273.893 StartY=121.137 StartZ=0 EndX=289.7 EndY=138.026 EndZ=0
    g1: LineSegment StartX=296.584 StartY=137.558 StartZ=0 EndX=296.584 EndY=111.577 EndZ=0
    g2: LineSegment StartX=297.084 StartY=111.577 StartZ=0 EndX=296.584 EndY=111.577 EndZ=0
    g3: LineSegment StartX=273.893 StartY=121.137 StartZ=0 EndX=273.528 EndY=121.478 EndZ=0
    g4: LineSegment StartX=297.084 StartY=140.558 StartZ=0 EndX=296.584 EndY=140.558 EndZ=0
    g5: LineSegment StartX=296.584 StartY=140.558 StartZ=0 EndX=296.584 EndY=137.558 EndZ=0
    g6: LineSegment StartX=291.385 StartY=140.558 StartZ=0 EndX=291.75 EndY=140.216 EndZ=0
    g7: LineSegment StartX=291.75 StartY=140.216 StartZ=0 EndX=289.7 EndY=138.026 EndZ=0
    g8: ArcOfCircle CenterX=286.283 CenterY=134.375 CenterZ=0 NormalX=0 NormalY=0 NormalZ=1 AngleXU=0 Radius=5 StartAngle=1.6e-15 EndAngle=0.818478
    g9: ArcOfCircle CenterX=296.584 CenterY=132.558 CenterZ=0 NormalX=0 NormalY=0 NormalZ=1 AngleXU=0 Radius=5 StartAngle=1.5708 EndAngle=3.14159
    g10: ArcOfCircle CenterX=296.584 CenterY=116.577 CenterZ=0 NormalX=0 NormalY=0 NormalZ=1 AngleXU=0 Radius=5 StartAngle=3.14159 EndAngle=4.71239
    g11: LineSegment StartX=291.584 StartY=116.577 StartZ=0 EndX=291.584 EndY=132.558 EndZ=0
    g12: LineSegment StartX=291.283 StartY=130.977 StartZ=0 EndX=291.283 EndY=134.375 EndZ=0
    g13: LineSegment StartX=273.893 StartY=121.137 StartZ=0 EndX=275.718 EndY=119.428 EndZ=0
    g14: LineSegment StartX=275.718 StartY=119.428 StartZ=0 EndX=280.28 EndY=119.428 EndZ=0
    g15: ArcOfCircle CenterX=280.28 CenterY=122.474 CenterZ=0 NormalX=0 NormalY=0 NormalZ=1 AngleXU=0 Radius=3.04602 StartAngle=4.71239 EndAngle=5.53087
    g16: ArcOfCircle CenterX=288.237 CenterY=130.977 CenterZ=0 NormalX=0 NormalY=0 NormalZ=1 AngleXU=0 Radius=3.04602 StartAngle=5.53087 EndAngle=6.28319
    g17: LineSegment StartX=282.503 StartY=120.393 StartZ=0 EndX=290.461 EndY=128.895 EndZ=0
  constraints (46):
    c: Coincident(g2,g-3)
    c: Coincident(g2,g1)
    c: Coincident(g3,g0)
    c: Coincident(g3,g-4)
    c: Perpendicular(g2,g-3)
    c: Perpendicular(g1,g2)
    c: Perpendicular(g0,g3)
    c: Perpendicular(g-4,g3)
    c: Equal(g2,g3)
    c: Distance(g3) = 0.5
    c: Coincident(g-3,g4)
    c: Coincident(g4,g5)
    c: Coincident(g5,g1)
    c: Coincident(g-4,g6)
    c: Coincident(g6,g7)
    c: Coincident(g7,g0)
    c: Parallel(g7,g0)
    c: Perpendicular(g6,g7)
    c: Parallel(g1,g5)
    c: Perpendicular(g4,g5)
    c: Equal(g5,g7)
    c: Distance(g7) = 3
    c: PointOnObject(g8,g0)
    c: Coincident(g8,g0)
    c: PointOnObject(g9,g1)
    c: Coincident(g9,g1)
    c: PointOnObject(g10,g1)
    c: Coincident(g10,g1)
    c: Tangent(g11,g9) = 1.5708
    c: Tangent(g11,g10) = 1.5708
    c: Tangent(g12,g8) = -1.5708
    c: Parallel(g11,g1)
    c: Equal(g8,g9)
    c: Radius(g9) = 5
    c: Coincident(g13,g0)
    c: Vertical(g12)
    c: Coincident(g13,g14)
    c: Horizontal(g14)
    c: Parallel(g13,g3)
    c: Distance(g13,g3) = 3
    c: Parallel(g17,g0)
    c: Tangent(g17,g16) = -1.5708
    c: Tangent(g14,g15) = -1.5708
    c: Tangent(g12,g16) = -1.5708
    c: Equal(g16,g15)
    c: Tangent(g17,g15) = -1.5708
FEATURE [PartDesign::Body] Body031
  Group = -> [Binder046,BaseBend012,Bend006,Sketch064]
  Origin = -> Origin038
  Tip = -> Bend006
COMPONENT P20 — recipe-attached ("Body032", modeled in this document).
Construction recipe (the document's own serialized feature program — sketch geometry with constraints, then the solid features built on it; lengths are millimeters unless a unit is written):

FEATURE [PartDesign::SubShapeBinder] Binder047
  BindCopyOnChange = 0
  BindMode = 0
  ClaimChildren = false
  Context = -> Body032 [Binder047.]
  Fuse = false
  MakeFace = true
  OffsetFill = false
  OffsetIntersection = false
  OffsetJoinType = 0
  OffsetOpenResult = false
  PartialLoad = false
  Relative = true
  Support = -> [Sketch001,Sketch049]
  _Version = 2
FEATURE [Sketcher::SketchObject] Sketch065
  ExternalGeometry = -> [Binder047]
  FullyConstrained = true
  MapMode = 5
  Support = -> [XY_Plane039]
  sketch-geometry (9):
    g0: LineSegment StartX=267.5 StartY=119.428 StartZ=0 EndX=269.69 EndY=117.378 EndZ=0
    g1: LineSegment StartX=269.69 StartY=117.378 StartZ=0 EndX=291.385 EndY=140.558 EndZ=0
    g2: LineSegment StartX=291.385 StartY=140.558 StartZ=0 EndX=297.084 EndY=140.558 EndZ=0
    g3: LineSegment StartX=297.084 StartY=140.558 StartZ=0 EndX=297.084 EndY=108.81 EndZ=0
    g4: LineSegment StartX=297.084 StartY=108.81 StartZ=0 EndX=300.084 EndY=108.81 EndZ=0
    g5: LineSegment StartX=290.084 StartY=143.558 StartZ=0 EndX=300.084 EndY=143.558 EndZ=0
    g6: LineSegment StartX=289.195 StartY=142.608 StartZ=0 EndX=291.385 EndY=140.558 EndZ=0
    g7: LineSegment StartX=291.385 StartY=140.558 StartZ=0 EndX=291.385 EndY=143.558 EndZ=0
    g8: LineSegment StartX=269.69 StartY=117.378 StartZ=0 EndX=297.084 EndY=108.81 EndZ=0
  constraints (25):
    c: Coincident(g-3,g0)
    c: Coincident(g0,g1)
    c: Coincident(g1,g2)
    c: Coincident(g2,g3)
    c: Coincident(g3,g4)
    c: PointOnObject(g4,g-5)
    c: Coincident(g5,g-4)
    c: Coincident(g5,g-5)
    c: Coincident(g6,g1)
    c: Coincident(g6,g7)
    c: PointOnObject(g7,g5)
    c: Perpendicular(g2,g7)
    c: Perpendicular(g5,g7)
    c: Perpendicular(g-4,g6)
    c: Perpendicular(g1,g6)
    c: Perpendicular(g1,g0)
    c: Perpendicular(g3,g4)
    c: Perpendicular(g-5,g4)
    c: PointOnObject(g6,g-4)
    c: Equal(g6,g7)
    c: Equal(g7,g4)
    c: Distance(g4) = 3
    c: Coincident(g8,g0)
    c: Equal(g1,g3)
    c: Coincident(g8,g3)
FEATURE [PartDesign::Pad] Pad016
  Direction = (0,0,1)
  Length = 40
  Length2 = 10
  Profile = -> Sketch065
  ReferenceAxis = -> Sketch065 [N_Axis]
  Type = 0
FEATURE [PartDesign::SubShapeBinder] Binder048
  BindCopyOnChange = 0
  BindMode = 0
  ClaimChildren = false
  Context = -> Body032 [Binder048.]
  Fuse = false
  MakeFace = true
  Offset = -4
  OffsetFill = false
  OffsetIntersection = false
  OffsetJoinType = 0
  OffsetOpenResult = false
  PartialLoad = false
  Placement = pos=(0,0,3) rot=(0,0,1;0rad)
  Relative = true
  Support = -> [Pad016[Sketch065.]]
  _Version = 2
FEATURE [PartDesign::Pocket] Pocket
  BaseFeature = -> Pad016
  Direction = (0,0,-1)
  Length = 5
  Length2 = 5
  Profile = -> Binder048
  Reversed = true
  Type = 0
FEATURE [Sketcher::SketchObject] Sketch066
  AttachmentOffset = pos=(0,0,3) rot=(0,0,1;0rad)
  ExternalGeometry = -> [Binder048]
  FullyConstrained = false
  MapMode = 5
  Placement = pos=(0,0,3) rot=(0,0,1;0rad)
  Support = -> [XY_Plane039]
  sketch-geometry (4):
    g0: LineSegment StartX=272.058 StartY=103.614 StartZ=0 EndX=288.179 EndY=98.5712 EndZ=0
    g1: LineSegment StartX=288.179 StartY=98.5712 StartZ=0 EndX=293.084 EndY=114.252 EndZ=0
    g2: LineSegment StartX=293.084 StartY=114.252 StartZ=0 EndX=276.963 EndY=119.295 EndZ=0
    g3: LineSegment StartX=276.963 StartY=119.295 StartZ=0 EndX=272.058 EndY=103.614 EndZ=0
  constraints (9):
    c: Coincident(g0,g1)
    c: Coincident(g1,g2)
    c: Coincident(g2,g3)
    c: Coincident(g3,g0)
    c: Parallel(g0,g2)
    c: Parallel(g1,g3)
    c: Perpendicular(g1,g0)
    c: Coincident(g1,g-3)
    c: Coincident(g2,g-3)
FEATURE [PartDesign::Pocket] Pocket015
  BaseFeature = -> Pocket
  Direction = (0,0,-1)
  Length = 5
  Length2 = 5
  Profile = -> Sketch066
  ReferenceAxis = -> Sketch066 [N_Axis]
  Refine = true
  Reversed = true
  Type = 0
FEATURE [PartDesign::Body] Body032
  Group = -> [Sketch065,Binder047,Pad016,Binder048,Pocket,Sketch066,Pocket015]
  Origin = -> Origin039
  Tip = -> Pocket015
COMPONENT P21 — recipe-attached ("sink", modeled in this document).
Construction recipe (the document's own serialized feature program — sketch geometry with constraints, then the solid features built on it; lengths are millimeters unless a unit is written):

FEATURE [PartDesign::SubShapeBinder] Binder007
  BindCopyOnChange = 0
  BindMode = 0
  ClaimChildren = true
  Context = -> Part [Body002.Binder007.]
  Fuse = false
  MakeFace = true
  OffsetFill = false
  OffsetIntersection = false
  OffsetJoinType = 0
  OffsetOpenResult = false
  PartialLoad = false
  Relative = false
  Support = -> [Compound006]
  _Version = 2
FEATURE [PartDesign::FeaturePython] BaseBend001  # WARN: FeaturePython — macro-defined, semantics opaque (R4)
  BendSide = 0
  BendSketch = -> Binder007
  MidPlane = true
  Placement = pos=(0,0,0) rot=(0.57735,0.57735,0.57735;2.0944rad)
  Reverse = false
  length = 600.168
  radius = 0.1
  thickness = 0.3
  expr: length = <<face_main_sketch>>.Constraints.width
FEATURE [PartDesign::SubShapeBinder] Binder008
  BindCopyOnChange = 0
  BindMode = 0
  ClaimChildren = true
  Context = -> Part [Body002.Binder008.]
  Fuse = false
  MakeFace = true
  OffsetFill = false
  OffsetIntersection = false
  OffsetJoinType = 0
  OffsetOpenResult = false
  PartialLoad = false
  Relative = true
  Support = -> [Body[BaseBend.Binder.Compound.Part__Mirroring.Compound004.Sketch001.]]
  _Version = 2
FEATURE [PartDesign::Mirrored] Mirrored003
  MirrorPlane = -> YZ_Plane002
  Placement = pos=(0,0,0) rot=(0.57735,0.57735,0.57735;2.0944rad)
FEATURE [PartDesign::Mirrored] Mirrored004
  MirrorPlane = -> XZ_Plane002
  Placement = pos=(0,0,0) rot=(0.57735,0.57735,0.57735;2.0944rad)
FEATURE [PartDesign::SubShapeBinder] Binder009
  BindCopyOnChange = 0
  BindMode = 0
  ClaimChildren = true
  Context = -> Part [Body004.Binder009.]
  Fuse = false
  MakeFace = true
  OffsetFill = false
  OffsetIntersection = false
  OffsetJoinType = 0
  OffsetOpenResult = false
  PartialLoad = false
  Relative = false
  Support = -> [Sketch001]
  _Version = 2
  expr: Support = <<face_main_sketch>>._self
FEATURE [PartDesign::Mirrored] Mirrored006
  MirrorPlane = -> YZ_Plane002
FEATURE [PartDesign::Mirrored] Mirrored007
  MirrorPlane = -> XZ_Plane002
FEATURE [Sketcher::SketchObject] Sketch023
  AttachmentOffset = pos=(175.72,0,0) rot=(0,1,0;0.818478rad)
  FullyConstrained = true
  MapMode = 5
  Placement = pos=(175.72,0,0) rot=(0.852419,0.369717,0.369717;1.7298rad)
  Support = -> [XZ_Plane002]
  expr: .AttachmentOffset.Base.x = Sketch013.Constraints.offset
  expr: .AttachmentOffset.Rotation.Angle = Sketch013.Constraints.angle
  expr: Constraints[9] = Sketch013.Constraints.angle
  sketch-geometry (7):
    g0: LineSegment StartX=-4.36e-14 StartY=0.4 StartZ=0 EndX=2.5 EndY=0.4 EndZ=0
    g1: LineSegment StartX=2.5 StartY=0.4 StartZ=0 EndX=49.2968 EndY=50.4 EndZ=0
    g2: LineSegment StartX=49.2968 StartY=50.4 StartZ=0 EndX=0 EndY=50.4 EndZ=0
    g3: LineSegment StartX=0 StartY=50.4 StartZ=0 EndX=-4.36e-14 EndY=0.4 EndZ=0
    g4: LineSegment StartX=2.5 StartY=0.4 StartZ=0 EndX=2.5 EndY=0 EndZ=0
    g5: LineSegment StartX=2.5 StartY=0 StartZ=0 EndX=0 EndY=0 EndZ=0
    g6: LineSegment StartX=0 StartY=0 StartZ=0 EndX=-4.36e-14 EndY=0.4 EndZ=0
  constraints (19):
    c: PointOnObject(g0,g-2)
    c: Horizontal(g0)
    c: Coincident(g0,g1)
    c: Coincident(g1,g2)
    c: PointOnObject(g2,g-2)
    c: Horizontal(g2)
    c: Coincident(g2,g3)
    c: Coincident(g3,g0)
    c: DistanceY(g0) = 0.4
    c: Angle(g1) = 0.818478
    c: DistanceY(g3,g3) = 50
    c: DistanceX(g0,g0) = 2.5
    c: Coincident(g1,g4)
    c: PointOnObject(g4,g-1)
    c: Vertical(g4)
    c: Coincident(g4,g5)
    c: Coincident(g5,g-1)
    c: Coincident(g5,g6)
    c: Coincident(g6,g3)
FEATURE [PartDesign::SubShapeBinder] Binder017
  BindCopyOnChange = 0
  BindMode = 0
  ClaimChildren = false
  Context = -> Part [Body010.Binder017.]
  Fuse = false
  MakeFace = true
  OffsetFill = false
  OffsetIntersection = false
  OffsetJoinType = 0
  OffsetOpenResult = false
  PartialLoad = false
  Relative = false
  Support = -> [Sketch001]
  _Version = 2
FEATURE [PartDesign::SubShapeBinder] Binder018
  BindCopyOnChange = 0
  BindMode = 0
  ClaimChildren = true
  Context = -> Part [Body010.Binder018.]
  Fuse = false
  MakeFace = true
  OffsetFill = false
  OffsetIntersection = false
  OffsetJoinType = 0
  OffsetOpenResult = false
  PartialLoad = false
  Relative = false
  Support = -> [Sketch027[Edge1]]
  _Version = 2
FEATURE [Sketcher::SketchObject] Sketch026
  ExternalGeometry = -> [Binder017,Binder018]
  FullyConstrained = true
  MapMode = 5
  Support = -> [XY_Plane011]
  sketch-geometry (4):
    g0: LineSegment StartX=176.816 StartY=0 StartZ=0 EndX=290.632 EndY=121.607 EndZ=0
    g1: LineSegment StartX=290.632 StartY=121.607 StartZ=0 EndX=297.084 EndY=121.607 EndZ=0
    g2: LineSegment StartX=297.084 StartY=121.607 StartZ=0 EndX=297.084 EndY=0 EndZ=0
    g3: LineSegment StartX=297.084 StartY=0 StartZ=0 EndX=176.816 EndY=0 EndZ=0
  constraints (12):
    c: PointOnObject(g0,g-1)
    c: Coincident(g1,g0)
    c: Horizontal(g1)
    c: Coincident(g2,g1)
    c: PointOnObject(g2,g-1)
    c: Vertical(g2)
    c: Coincident(g3,g2)
    c: Coincident(g3,g0)
    c: DistanceX(g2,g-3) = 3
    c: Parallel(g0,g-4)
    c: Horizontal(g0,g-4)
    c: Distance(g0,g-4) = 0.4
FEATURE [PartDesign::Pad] Pad006
  Direction = (0,0,1)
  Length = 0.3
  Length2 = 10
  Profile = -> Sketch026
  ReferenceAxis = -> Sketch026 [N_Axis]
  Type = 0
FEATURE [PartDesign::Mirrored] Mirrored008
  BaseFeature = -> Pad006
  MirrorPlane = -> XZ_Plane011
  Originals = -> [Pad006]
  Refine = true
FEATURE [PartDesign::FeaturePython] Bend003  # WARN: FeaturePython — macro-defined, semantics opaque (R4)
  AutoMiter = false
  BaseFeature = -> Mirrored008
  BendType = 0
  LengthList = [20]
  LengthSpec = 0
  ReliefFactor = 0.7
  UseReliefFactor = false
  angle = 90
  baseObject = -> Mirrored008 [Edge6,Edge3]
  bendAList = [90]
  extend1 = 0
  extend2 = 0
  gap1 = 3
  gap2 = 0
  invert = false
  kfactor = 0.5
  length = 20
  maxExtendDist = 5
  minGap = 0.1
  minReliefGap = 1
  miterangle1 = 0
  miterangle2 = 0
  offset = 0
  radius = 0.1
  reliefType = 0
  reliefd = 1
  reliefw = 0.8
  sketchflip = false
  sketchinvert = false
  unfold = false
FEATURE [PartDesign::SubShapeBinder] Binder019
  BindCopyOnChange = 0
  BindMode = 0
  ClaimChildren = true
  Context = -> Part [Body002.Binder019.]
  Fuse = false
  MakeFace = true
  OffsetFill = false
  OffsetIntersection = false
  OffsetJoinType = 0
  OffsetOpenResult = false
  PartialLoad = false
  Relative = false
  Support = -> [Sketch027]
  _Version = 2
FEATURE [Sketcher::SketchObject] Sketch013
  ExternalGeometry = -> [Binder008,Binder019]
  FullyConstrained = true
  MapMode = 5
  Support = -> [XY_Plane002]
  expr: Constraints[34] = <<top_base_sketch>>.Constraints.angle
  expr: Constraints[9] = <<face_main_sketch>>.Constraints.width / 2
  sketch-geometry (17):
    g0: LineSegment StartX=164.614 StartY=9.5 StartZ=0 EndX=175.274 EndY=-0.476667 EndZ=0
    g1: LineSegment StartX=290.084 StartY=143.558 StartZ=0 EndX=300.743 EndY=133.581 EndZ=0
    g2: LineSegment StartX=175.72 StartY=0 StartZ=0 EndX=300.084 EndY=0 EndZ=0
    g3: LineSegment StartX=300.084 StartY=0 StartZ=0 EndX=300.084 EndY=132.877 EndZ=0
    g4: LineSegment StartX=300.743 StartY=133.581 StartZ=0 EndX=300.084 EndY=132.877 EndZ=0
    g5: LineSegment StartX=300.084 StartY=132.877 StartZ=0 EndX=290.084 EndY=122.192 EndZ=0
    g6: LineSegment StartX=290.084 StartY=163.558 StartZ=0 EndX=300.084 EndY=163.558 EndZ=0
    g7: LineSegment StartX=300.084 StartY=163.558 StartZ=0 EndX=300.084 EndY=132.877 EndZ=0
    g8: LineSegment StartX=290.084 StartY=122.192 StartZ=0 EndX=175.72 EndY=0 EndZ=0
    g9: LineSegment StartX=175.72 StartY=0 StartZ=0 EndX=175.274 EndY=-0.476667 EndZ=0
    g10: ArcOfCircle CenterX=289.748 CenterY=143.158 CenterZ=0 NormalX=0 NormalY=0 NormalZ=1 AngleXU=0 Radius=0.4 StartAngle=0.174533 EndAngle=1.57079
    g11: LineSegment StartX=289.748 StartY=143.558 StartZ=0 EndX=290.084 EndY=143.558 EndZ=0
    g12: LineSegment StartX=290.142 StartY=143.227 StartZ=0 EndX=290.084 EndY=143.558 EndZ=0
    g13: LineSegment StartX=290.084 StartY=163.558 StartZ=0 EndX=290.084 EndY=143.222 EndZ=0
    g14: LineSegment StartX=290.084 StartY=143.222 StartZ=0 EndX=290.084 EndY=122.192 EndZ=0
    g15: ArcOfCircle CenterX=290.084 CenterY=143.558 CenterZ=0 NormalX=0 NormalY=0 NormalZ=1 AngleXU=0 Radius=0.33564 StartAngle=4.71239 EndAngle=4.88692
    g16: GeomPoint X=177.405 Y=1.8 Z=0
  constraints (48):
    c: Coincident(g0,g-3)
    c: Coincident(g0,g9)
    c: Perpendicular(g-3,g0)
    c: Coincident(g1,g4)
    c: Perpendicular(g-3,g1)
    c: PointOnObject(g2,g-1)
    c: PointOnObject(g2,g-1)
    c: Coincident(g2,g3)
    c: Vertical(g3)
    c: DistanceX(g2) = 300.084
    c: Coincident(g4,g5)
    c: Parallel(g4,g-3)
    c: Coincident(g4,g3)
    c: Coincident(g5,g8)
    c: Parallel(g5,g-3)
    c: Coincident(g5,g14)
    c: Coincident(g6,g13)
    c: Horizontal(g6)
    c: Coincident(g7,g6)
    c: Coincident(g7,g3)
    c: Vertical(g7)
    c: DistanceY(g1,g13) = 20
    c: Coincident(g8,g9)
    c: Parallel(g8,g-3)
    c: Parallel(g9,g-3)
    c: Coincident(g8,g2)
    c: Radius(g10) = 0.4
    c: Coincident(g11,g10)
    c: Tangent(g11,g10)
    c: Coincident(g12,g11)
    c: Tangent(g12,g10) = -1.5708
    c: Coincident(g1,g-3)
    c: Coincident(g11,g1)
    c: Horizontal(g11)
    c: Angle(g11,g12) = 1.74533
    c: Coincident(g13,g14)
    c: Vertical(g13)
    c: Vertical(g14)
    c: PointOnObject(g1,g13)
    c: Coincident(g15,g1)
    c: Coincident(g15,g10)
    c: Coincident(g15,g13)
    c: Angle(g2,g8) = 0.818478  'angle'
    c: DistanceX(g2) = 175.72  'offset'
    c: PointOnObject(g16,g8)
    c: Distance(g16,g2) = 1.8
    c: Distance(g16,g2) = 2.46539
    c: Distance(g-4,g8) = 0.4
FEATURE [PartDesign::Pocket] Pocket003
  BaseFeature = -> BaseBend001
  Direction = (0,0,-1)
  Length = 5
  Length2 = 5
  Midplane = true
  Placement = pos=(0,0,0) rot=(0.57735,0.57735,0.57735;2.0944rad)
  Profile = -> Sketch013
  ReferenceAxis = -> Sketch013 [N_Axis]
  Type = 1
FEATURE [PartDesign::MultiTransform] MultiTransform
  BaseFeature = -> Pocket003
  Originals = -> [Pocket003]
  Placement = pos=(0,0,0) rot=(0.57735,0.57735,0.57735;2.0944rad)
  Transformations = -> [Mirrored003,Mirrored004]
FEATURE [PartDesign::FeaturePython] Bend001  # WARN: FeaturePython — macro-defined, semantics opaque (R4)
  AutoMiter = true
  BaseFeature = -> MultiTransform
  BendType = 0
  LengthList = [20]
  LengthSpec = 0
  ReliefFactor = 0.7
  UseReliefFactor = false
  angle = 90
  baseObject = -> MultiTransform [Edge19,Edge25,Edge33,Edge34,Edge24,Edge27,Edge36,Edge35]
  bendAList = [90]
  extend1 = 0
  extend2 = 0
  gap1 = 0
  gap2 = 0
  invert = false
  kfactor = 0.5
  length = 20
  maxExtendDist = 5
  minGap = 0.1
  minReliefGap = 1
  miterangle1 = 0
  miterangle2 = 0
  offset = 0
  radius = 0.1
  reliefType = 0
  reliefd = 1
  reliefw = 0.8
  sketchflip = false
  sketchinvert = false
  unfold = false
  expr: radius = BaseBend001.radius
FEATURE [Sketcher::SketchObject] Sketch022
  ExternalGeometry = -> [Sketch013,Binder008]
  FullyConstrained = true
  MapMode = 5
  Support = -> [XY_Plane002]
  sketch-geometry (12):
    g0: LineSegment StartX=289.382 StartY=121.442 StartZ=0 EndX=289.674 EndY=121.169 EndZ=0
    g1: LineSegment StartX=289.674 StartY=121.169 StartZ=0 EndX=290.484 EndY=122.034 EndZ=0
    g2: LineSegment StartX=290.484 StartY=122.034 StartZ=0 EndX=290.484 EndY=123.219 EndZ=0
    g3: LineSegment StartX=290.484 StartY=123.219 StartZ=0 EndX=290.084 EndY=123.219 EndZ=0
    g4: LineSegment StartX=289.382 StartY=121.442 StartZ=0 EndX=287.484 EndY=123.219 EndZ=0
    g5: LineSegment StartX=287.484 StartY=123.219 StartZ=0 EndX=290.084 EndY=123.219 EndZ=0
    g6: LineSegment StartX=290.084 StartY=123.219 StartZ=0 EndX=290.084 EndY=122.192 EndZ=0
    g7: LineSegment StartX=290.084 StartY=122.192 StartZ=0 EndX=289.382 EndY=121.442 EndZ=0
    g8: LineSegment StartX=290.084 StartY=140.558 StartZ=0 EndX=290.484 EndY=140.558 EndZ=0
    g9: LineSegment StartX=290.484 StartY=140.558 StartZ=0 EndX=290.484 EndY=143.558 EndZ=0
    g10: LineSegment StartX=290.484 StartY=143.558 StartZ=0 EndX=290.084 EndY=143.558 EndZ=0
    g11: LineSegment StartX=290.084 StartY=143.558 StartZ=0 EndX=290.084 EndY=140.558 EndZ=0
  constraints (34):
    c: Coincident(g0,g1)
    c: Coincident(g1,g2)
    c: Vertical(g2)
    c: Coincident(g2,g3)
    c: Perpendicular(g-3,g0)
    c: Horizontal(g3)
    c: Equal(g3,g0)
    c: Equal(g1,g2)
    c: DistanceX(g3,g3) = 0.4
    c: PointOnObject(g4,g-3)
    c: Coincident(g4,g5)
    c: Horizontal(g5)
    c: Perpendicular(g-3,g4)
    c: Equal(g4,g5)
    c: DistanceX(g5,g5) = 2.6
    c: Coincident(g3,g5)
    c: Vertical(g3,g-3)
    c: Coincident(g0,g4)
    c: Coincident(g6,g3)
    c: Coincident(g7,g6)
    c: Coincident(g7,g0)
    c: Coincident(g6,g-3)
    c: Coincident(g8,g9)
    c: Coincident(g9,g10)
    c: Coincident(g10,g11)
    c: Coincident(g11,g8)
    c: Horizontal(g8)
    c: Horizontal(g10)
    c: Vertical(g9)
    c: Vertical(g11)
    c: Horizontal(g10,g-4)
    c: Equal(g8,g3)
    c: Vertical(g8,g3)
    c: DistanceY(g11,g11) = 3
FEATURE [PartDesign::Pocket] Pocket005
  BaseFeature = -> Bend001
  Direction = (0,0,-1)
  Length = 5
  Length2 = 5
  Midplane = true
  Profile = -> Sketch022
  ReferenceAxis = -> Sketch022 [N_Axis]
  Type = 1
FEATURE [PartDesign::Pocket] Pocket006
  BaseFeature = -> Pocket005
  Direction = (-0.730107,0.683333,-1e-16)
  Length = 0.4
  Length2 = 5
  Profile = -> Sketch023
  ReferenceAxis = -> Sketch023 [N_Axis]
  Reversed = true
  Type = 0
FEATURE [PartDesign::MultiTransform] MultiTransform001
  BaseFeature = -> Pocket006
  Originals = -> [Pocket005,Pocket006]
  Transformations = -> [Mirrored006,Mirrored007]
FEATURE [PartDesign::Boolean] Boolean008
  BaseFeature = -> Bend003
  Group = -> [Compound017]
  Type = 1
FEATURE [PartDesign::Body] Body010  label="top_supplement_material_0.30ansi"
  Group = -> [Sketch026,Binder017,Pad006,Mirrored008,Bend003,Boolean008,Binder018]
  Origin = -> Origin011
  Tip = -> Boolean008
FEATURE [PartDesign::SubShapeBinder] Binder024
  BindCopyOnChange = 0
  BindMode = 0
  ClaimChildren = true
  Context = -> Part [Body004.Binder024.]
  Fuse = false
  MakeFace = true
  OffsetFill = false
  OffsetIntersection = false
  OffsetJoinType = 0
  OffsetOpenResult = false
  PartialLoad = false
  Relative = false
  Support = -> [Sketch027]
  _Version = 2
FEATURE [Sketcher::SketchObject] Sketch014
  ExternalGeometry = -> [Binder009,Binder024]
  FullyConstrained = false
  MapMode = 5
  Support = -> [XY_Plane005]
  sketch-geometry (15):
    g0: LineSegment StartX=0 StartY=0 StartZ=0 EndX=167.821 EndY=0 EndZ=0
    g1: LineSegment StartX=175.123 StartY=3.16667 StartZ=0 EndX=276.972 EndY=111.987 EndZ=0
    g2: LineSegment StartX=269.671 StartY=128.821 StartZ=0 EndX=224.007 EndY=128.821 EndZ=0
    g3: LineSegment StartX=216.706 StartY=125.654 StartZ=0 EndX=146.055 EndY=50.1667 EndZ=0
    g4: LineSegment StartX=138.754 StartY=47 StartZ=0 EndX=0 EndY=47 EndZ=0
    g5: LineSegment StartX=0 StartY=47 StartZ=0 EndX=0 EndY=0 EndZ=0
    g6: ArcOfCircle CenterX=138.754 CenterY=57 CenterZ=0 NormalX=0 NormalY=0 NormalZ=1 AngleXU=0 Radius=10 StartAngle=4.71239 EndAngle=5.53087
    g7: GeomPoint X=143.091 Y=47 Z=0
    g8: ArcOfCircle CenterX=224.007 CenterY=118.821 CenterZ=0 NormalX=0 NormalY=0 NormalZ=1 AngleXU=0 Radius=10 StartAngle=1.5708 EndAngle=2.38927
    g9: GeomPoint X=219.67 Y=128.821 Z=0
    g10: ArcOfCircle CenterX=167.821 CenterY=10 CenterZ=0 NormalX=0 NormalY=0 NormalZ=1 AngleXU=0 Radius=10 StartAngle=4.71239 EndAngle=5.53087
    g11: GeomPoint X=172.159 Y=0 Z=0
    g12: ArcOfCircle CenterX=269.671 CenterY=118.821 CenterZ=0 NormalX=0 NormalY=0 NormalZ=1 AngleXU=0 Radius=10 StartAngle=5.53087 EndAngle=7.85398
    g13: GeomPoint X=292.727 Y=128.821 Z=0
    g14: Circle CenterX=0 CenterY=0 CenterZ=0 NormalX=0 NormalY=0 NormalZ=1 AngleXU=0 Radius=10
  constraints (34):
    c: PointOnObject(g0,g-2)
    c: Horizontal(g0)
    c: Horizontal(g2)
    c: PointOnObject(g4,g-2)
    c: Horizontal(g4)
    c: Coincident(g4,g5)
    c: Coincident(g5,g0)
    c: PointOnObject(g7,g3)
    c: PointOnObject(g7,g4)
    c: Tangent(g3,g6) = 1.5708
    c: Tangent(g4,g6) = 1.5708
    c: PointOnObject(g9,g2)
    c: PointOnObject(g9,g3)
    c: Tangent(g2,g8) = -1.5708
    c: Tangent(g3,g8) = -1.5708
    c: PointOnObject(g11,g0)
    c: PointOnObject(g11,g1)
    c: Tangent(g0,g10) = -1.5708
    c: Tangent(g1,g10) = -1.5708
    c: PointOnObject(g13,g1)
    c: PointOnObject(g13,g2)
    c: Tangent(g1,g12) = -1.5708
    c: Tangent(g2,g12) = -1.5708
    c: Equal(g14,g6)
    c: Equal(g14,g8)
    c: Equal(g14,g12)
    c: Equal(g14,g10)
    c: Radius(g14) = 10
    c: Parallel(g1,g-3)
    c: Parallel(g-3,g3)
    c: Coincident(g14,g-1)
    c: DistanceY(g5,g5) = 47
    c: PointOnObject(g0,g-1)
    c: Distance(g11,g-4) = 3
FEATURE [PartDesign::Pad] Pad
  Direction = (0,0,1)
  Length = 5
  Length2 = 10
  Profile = -> Sketch014
  ReferenceAxis = -> Sketch014 [N_Axis]
  Type = 0
FEATURE [PartDesign::Mirrored] Mirrored005
  BaseFeature = -> Pad
  MirrorPlane = -> Sketch014 [V_Axis]
  Originals = -> [Pad]
  Refine = true
FEATURE [Part::MultiFuse] Fusion  label="top_fix_cut1"
  Refine = true
  Shapes = -> [Populate004,Populate003,Populate007,Populate049,Cylinder005]
FEATURE [PartDesign::FeatureSubtractivePython] PDW_Sub  # link proxy (typed FeaturePython)
  BaseFeature = -> Mirrored005
  Body = Body004
  ClaimChildren = true
  EditPlacementAdjustments = false
  Enabled = 0
  LinkedObject = -> Fusion
  MeshTolerance = 0.1
  PatternBase = -> Fusion
  PatternBaseOffset = 0
  PatternBaseScale = 1
  PatternBaseScaleXYZ = (1,1,1)
  PatternOffsetCut = false
  PatternOffsetIntersection = false
  PatternOffsetJoin = 0
  PatternOffsetMode = 0
  PatternOffsetSelfIntersection = false
  PatternOperation = 0
  PatternOperationDefault = None
  PatternScaleCut = false
  PatternShapeOffset = 0
  PatternShapeScale = 1
  PatternShapeScaleXYZ = (1,1,1)
  PatternToolOffset = 0
  PatternToolScale = 1
  PatternToolScaleXYZ = (1,1,1)
  Refine = true
  RefineMesh = true
  ShapeManagement = 1
  ShowMeshProps = false
  ShowOffsetProps = false
  ShowScaleProps = false
  ShowWarnings = true
  TipBase = -> Mirrored005
  TipBaseOffset = 0
  TipBaseScale = 1
  TipBaseScaleXYZ = (1,1,1)
  TipOffsetCut = false
  TipOffsetIntersection = false
  TipOffsetJoin = 0
  TipOffsetMode = 0
  TipOffsetSelfIntersection = false
  TipOperation = 1
  TipOperationDefault = Cut
  TipScaleCut = false
  TipShapeOffset = 0
  TipShapeScale = 1
  TipShapeScaleXYZ = (1,1,1)
  TipTool = -> Fusion
  TipToolOffset = 0
  TipToolScale = 1
  TipToolScaleXYZ = (1,1,1)
  Type = Subtractive
  UsePatternBaseAddSubShape = false
  UsePatternToolAddSubShape = false
  UseTipBaseAddSubShape = false
  UseTipToolAddSubShape = false
  Version = 0.2023.08.13
FEATURE [PartDesign::Boolean] Boolean004
  BaseFeature = -> MultiTransform001
  Group = -> [Compound007]
  Refine = true
  Type = 1
FEATURE [PartDesign::Body] Body002  label="top_material_0.30ansi"
  Group = -> [Binder007,BaseBend001,Binder008,Sketch013,Binder019,Pocket003,MultiTransform,Mirrored003,Mirrored004,Bend001,Sketch022,Pocket005,Sketch023,Pocket006,MultiTransform001,Mirrored006,Mirrored007,Boolean004]
  Origin = -> Origin002
  Tip = -> Boolean004
FEATURE [PartDesign::FeatureBase] BaseFeature002
  BaseFeature = -> PDW_Sub
FEATURE [PartDesign::Boolean] Boolean005
  BaseFeature = -> PDW_Sub
  Group = -> [Populate015]
  Type = 1
FEATURE [PartDesign::Body] Body004  label="top_fix"
  Group = -> [Sketch014,Binder009,Pad,Binder024,Mirrored005,PDW_Sub,Fusion,Boolean005]
  Origin = -> Origin005
  Placement = pos=(0,0,3) rot=(0,0,1;0rad)
  Tip = -> Boolean005
FEATURE [PartDesign::Boolean] Boolean006
  BaseFeature = -> BaseFeature002
  Group = -> [Compound013]
  Type = 1
FEATURE [PartDesign::Body] Body009  label="top_fix2"
  BaseFeature = -> PDW_Sub
  Group = -> [BaseFeature002,Boolean006]
  Origin = -> Origin010
  Placement = pos=(0,0,3) rot=(0,0,1;3.14159rad)
  Tip = -> Boolean006
  expr: BaseFeature = <<PDW_Sub>>._self
COMPONENT P22 — recipe-attached ("Body028", modeled in this document).
Construction recipe (the document's own serialized feature program — sketch geometry with constraints, then the solid features built on it; lengths are millimeters unless a unit is written):

FEATURE [PartDesign::SubShapeBinder] Binder
  BindCopyOnChange = 0
  BindMode = 0
  ClaimChildren = true
  Context = -> Body006 [Body.Binder.]
  Fuse = false
  MakeFace = true
  OffsetFill = false
  OffsetIntersection = false
  OffsetJoinType = 0
  OffsetOpenResult = false
  PartialLoad = false
  Relative = true
  Support = -> [Compound]
  _Version = 2
FEATURE [PartDesign::FeaturePython] BaseBend  label="face_BaseBend"  # WARN: FeaturePython — macro-defined, semantics opaque (R4)
  BendSide = 0
  BendSketch = -> Binder
  MidPlane = false
  Reverse = false
  length = 640
  radius = 0.1
  thickness = 0.3
  expr: radius = composit_properties#<<Properties>>.bend_r
  expr: thickness = composit_properties#<<Properties>>.al_thickness
FEATURE [PartDesign::SubShapeBinder] Binder002
  BindCopyOnChange = 0
  BindMode = 0
  ClaimChildren = false
  Context = -> Body006 [Body.Binder002.]
  Fuse = false
  MakeFace = true
  OffsetFill = false
  OffsetIntersection = false
  OffsetJoinType = 0
  OffsetOpenResult = false
  PartialLoad = false
  Relative = true
  Support = -> [Sketch]
  _Version = 2
FEATURE [Sketcher::SketchObject] Sketch007
  ExternalGeometry = -> [Binder002]
  FullyConstrained = true
  MapMode = 5
  Support = -> [XY_Plane]
  expr: Constraints[5] = <<face_BaseBend>>.thickness
  expr: Constraints[9] = <<face_main_sketch>>.Constraints.offset
  sketch-geometry (7):
    g0: LineSegment StartX=-267.5 StartY=119.428 StartZ=0 EndX=267.5 EndY=119.428 EndZ=0
    g1: LineSegment StartX=267.5 StartY=119.428 StartZ=0 EndX=267.719 EndY=119.223 EndZ=0
    g2: LineSegment StartX=267.719 StartY=119.223 StartZ=0 EndX=267.719 EndY=0 EndZ=0
    g3: LineSegment StartX=267.719 StartY=0 StartZ=0 EndX=-267.719 EndY=0 EndZ=0
    g4: LineSegment StartX=267.5 StartY=119.428 StartZ=0 EndX=267.5 EndY=109.928 EndZ=0
    g5: LineSegment StartX=-267.5 StartY=119.428 StartZ=0 EndX=-267.719 EndY=119.223 EndZ=0
    g6: LineSegment StartX=-267.719 StartY=119.223 StartZ=0 EndX=-267.719 EndY=0 EndZ=0
  constraints (19):
    c: Coincident(g0,g1)
    c: Coincident(g1,g2)
    c: PointOnObject(g2,g-1)
    c: Vertical(g2)
    c: Coincident(g2,g3)
    c: Distance(g1) = 0.3
    c: Coincident(g4,g0)
    c: PointOnObject(g4,g-3)
    c: Vertical(g4)
    c: DistanceY(g4,g4) = 9.5
    c: DistanceX(g0) = 267.5
    c: Coincident(g0,g5)
    c: Coincident(g5,g6)
    c: PointOnObject(g6,g-1)
    c: Coincident(g3,g6)
    c: Vertical(g6)
    c: Symmetric(g0,g0,g-2)
    c: Symmetric(g5,g1,g-2)
    c: Perpendicular(g-3,g1)
FEATURE [Sketcher::SketchObject] Sketch009
  FullyConstrained = true
  MapMode = 5
  Support = -> [XY_Plane]
FEATURE [PartDesign::FeaturePython] Extend  # WARN: FeaturePython — macro-defined, semantics opaque (R4)
  BaseFeature = -> BaseBend
  Offset = 0.02
  Refine = true
  UseSubtraction = false
  baseObject = -> BaseBend [Face1]
  gap1 = 0
  gap2 = 0
  length = 0
  expr: baseObject = tuple(<<face_BaseBend>>._self; <<Face1>>)
FEATURE [PartDesign::FeaturePython] Bend  # WARN: FeaturePython — macro-defined, semantics opaque (R4)
  AutoMiter = false
  BaseFeature = -> Extend
  BendType = 0
  LengthList = [0.1]
  LengthSpec = 0
  ReliefFactor = 0.7
  UseReliefFactor = false
  angle = 90
  baseObject = -> Extend [Edge18,Edge50,Edge139,Edge78,Edge112]
  bendAList = [90]
  extend1 = 0
  extend2 = 0
  gap1 = 0
  gap2 = 0
  invert = false
  kfactor = 0.5
  length = 0.1
  maxExtendDist = 5
  minGap = 0.1
  minReliefGap = 1
  miterangle1 = 0
  miterangle2 = 0
  offset = 0
  radius = 0.1
  reliefType = 0
  reliefd = 1
  reliefw = 0.8
  sketchflip = false
  sketchinvert = false
  unfold = false
  expr: radius = <<face_BaseBend>>.radius
FEATURE [PartDesign::SubShapeBinder] Binder006
  BindCopyOnChange = 0
  BindMode = 0
  ClaimChildren = true
  Context = -> Body006 [Body.Binder006.]
  Fuse = false
  MakeFace = true
  OffsetFill = false
  OffsetIntersection = false
  OffsetJoinType = 0
  OffsetOpenResult = false
  PartialLoad = false
  Relative = true
  Support = -> [BaseBend[Binder.Compound.Compound004.Sketch001.]]
  _Version = 2
FEATURE [PartDesign::CoordinateSystem] Local_CS
  AttacherType = Attacher::AttachEngine3D
  AttachmentOffset = pos=(0,0,640) rot=(0,0,1;0rad)
  MapMode = 5
  Placement = pos=(0,0,640) rot=(0,0,1;0rad)
  Support = -> [XY_Plane]
  expr: .AttachmentOffset.Base.z = <<face_BaseBend>>.length
FEATURE [PartDesign::SubShapeBinder] Binder011
  BindCopyOnChange = 0
  BindMode = 0
  ClaimChildren = true
  Context = -> Body [Binder011.]
  Fuse = false
  MakeFace = true
  OffsetFill = false
  OffsetIntersection = false
  OffsetJoinType = 0
  OffsetOpenResult = false
  PartialLoad = false
  Relative = false
  Support = -> [Link001[Body001.Line.Edge1,Body001.Line002.Edge1,Body001.Line003.Edge1]]
  _Version = 2
FEATURE [PartDesign::SubShapeBinder] Binder021
  BindCopyOnChange = 0
  BindMode = 0
  ClaimChildren = true
  Context = -> Body [Binder021.]
  Fuse = false
  MakeFace = true
  OffsetFill = false
  OffsetIntersection = false
  OffsetJoinType = 0
  OffsetOpenResult = false
  PartialLoad = false
  Relative = true
  Support = -> [Sketch028]
  _Version = 2
FEATURE [Sketcher::SketchObject] Sketch017
  ExternalGeometry = -> [Binder021,Binder]
  FullyConstrained = true
  MapMode = 5
  Placement = pos=(0,0,640) rot=(0,0,1;0rad)
  Support = -> [Local_CS]
  sketch-geometry (20):
    g0: LineSegment StartX=164.614 StartY=9.5 StartZ=0 EndX=164.979 EndY=9.15833 EndZ=0
    g1: LineSegment StartX=164.979 StartY=9.15833 StartZ=0 EndX=174.186 EndY=18.9956 EndZ=0
    g2: LineSegment StartX=174.186 StartY=18.9956 StartZ=0 EndX=173.821 EndY=19.3372 EndZ=0
    g3: LineSegment StartX=173.821 StartY=19.3372 StartZ=0 EndX=164.614 EndY=9.5 EndZ=0
    g4: LineSegment StartX=121.161 StartY=9 StartZ=0 EndX=164.614 EndY=9 EndZ=0
    g5: LineSegment StartX=164.614 StartY=9 StartZ=0 EndX=164.614 EndY=9.5 EndZ=0
    g6: LineSegment StartX=164.614 StartY=9.5 StartZ=0 EndX=121.161 EndY=9.5 EndZ=0
    g7: LineSegment StartX=121.161 StartY=9.5 StartZ=0 EndX=121.161 EndY=9 EndZ=0
    g8: LineSegment StartX=299.584 StartY=140.558 StartZ=0 EndX=300.084 EndY=140.558 EndZ=0
    g9: LineSegment StartX=300.084 StartY=140.558 StartZ=0 EndX=300.084 EndY=143.558 EndZ=0
    g10: LineSegment StartX=300.084 StartY=143.558 StartZ=0 EndX=299.584 EndY=143.558 EndZ=0
    g11: LineSegment StartX=299.584 StartY=143.558 StartZ=0 EndX=299.584 EndY=140.558 EndZ=0
    g12: LineSegment StartX=299.584 StartY=0.5 StartZ=0 EndX=300.084 EndY=0.5 EndZ=0
    g13: LineSegment StartX=300.084 StartY=0.5 StartZ=0 EndX=300.084 EndY=1e-16 EndZ=0
    g14: LineSegment StartX=300.084 StartY=1e-16 StartZ=0 EndX=299.584 EndY=0 EndZ=0
    g15: LineSegment StartX=299.584 StartY=0 StartZ=0 EndX=299.584 EndY=0.5 EndZ=0
    g16: LineSegment StartX=276.588 StartY=129.139 StartZ=0 EndX=276.953 EndY=128.797 EndZ=0
    g17: LineSegment StartX=276.953 StartY=128.797 StartZ=0 EndX=290.449 EndY=143.216 EndZ=0
    g18: LineSegment StartX=290.449 StartY=143.216 StartZ=0 EndX=290.084 EndY=143.558 EndZ=0
    g19: LineSegment StartX=290.084 StartY=143.558 StartZ=0 EndX=276.588 EndY=129.139 EndZ=0
  constraints (49):
    c: Coincident(g6,g7)
    c: Coincident(g4,g7)
    c: Coincident(g0,g3)
    c: Coincident(g3,g5)
    c: Coincident(g5,g6)
    c: Coincident(g4,g5)
    c: Coincident(g0,g1)
    c: Coincident(g2,g3)
    c: Coincident(g1,g2)
    c: Coincident(g16,g19)
    c: Coincident(g16,g17)
    c: Coincident(g18,g19)
    c: Coincident(g17,g18)
    c: Coincident(g14,g15)
    c: Coincident(g12,g15)
    c: Coincident(g8,g11)
    c: Coincident(g10,g11)
    c: Coincident(g13,g14)
    c: Coincident(g12,g13)
    c: Coincident(g8,g9)
    c: Coincident(g9,g10)
    c: Perpendicular(g19,g18)
    c: Perpendicular(g17,g18)
    c: Perpendicular(g16,g17)
    c: Perpendicular(g10,g9)
    c: Perpendicular(g11,g10)
    c: Perpendicular(g9,g8)
    c: Perpendicular(g12,g13)
    c: Perpendicular(g15,g12)
    c: Perpendicular(g14,g13)
    c: Coincident(g12,g-6)
    c: Coincident(g12,g-6)
    c: PointOnObject(g14,g-1)
    c: Coincident(g6,g-7)
    c: Coincident(g4,g-7)
    c: Perpendicular(g6,g7)
    c: Perpendicular(g4,g7)
    c: Perpendicular(g5,g6)
    c: Coincident(g2,g-3)
    c: Coincident(g1,g-3)
    c: Perpendicular(g3,g2)
    c: Perpendicular(g2,g1)
    c: Perpendicular(g3,g0)
    c: Coincident(g16,g-4)
    c: Coincident(g16,g-4)
    c: Coincident(g8,g-5)
    c: Coincident(g8,g-5)
    c: PointOnObject(g18,g-8)
    c: PointOnObject(g10,g-8)
FEATURE [Sketcher::SketchObject] Sketch019
  AttachmentOffset = pos=(0,0,0.1) rot=(0,0,1;0rad)
  ExternalGeometry = -> [Binder021]
  FullyConstrained = true
  MapMode = 5
  Placement = pos=(0,0,640.1) rot=(0,0,1;0rad)
  Support = -> [Local_CS]
  sketch-geometry (12):
    g0: ArcOfCircle CenterX=112.161 CenterY=9 CenterZ=0 NormalX=0 NormalY=0 NormalZ=1 AngleXU=0 Radius=9 StartAngle=4.71239 EndAngle=6.28319
    g1: LineSegment StartX=112.161 StartY=0 StartZ=0 EndX=0 EndY=0 EndZ=0
    g2: LineSegment StartX=121.161 StartY=9 StartZ=0 EndX=0 EndY=9 EndZ=0
    g3: LineSegment StartX=0 StartY=9 StartZ=0 EndX=0 EndY=0 EndZ=0
    g4: LineSegment StartX=299.584 StartY=0.5 StartZ=0 EndX=299.584 EndY=140.558 EndZ=0
    g5: LineSegment StartX=276.953 StartY=128.797 StartZ=0 EndX=174.186 EndY=18.9956 EndZ=0
    g6: ArcOfCircle CenterX=181.02 CenterY=26.2966 CenterZ=0 NormalX=0 NormalY=0 NormalZ=1 AngleXU=0 Radius=10 StartAngle=3.96007 EndAngle=5.53087
    g7: ArcOfCircle CenterX=270.12 CenterY=121.496 CenterZ=0 NormalX=0 NormalY=0 NormalZ=1 AngleXU=0 Radius=10 StartAngle=5.53087 EndAngle=7.10166
    g8: ArcOfCircle CenterX=299.584 CenterY=130.558 CenterZ=0 NormalX=0 NormalY=0 NormalZ=1 AngleXU=0 Radius=10 StartAngle=1.5708 EndAngle=3.14159
    g9: ArcOfCircle CenterX=299.584 CenterY=10.5 CenterZ=0 NormalX=0 NormalY=0 NormalZ=1 AngleXU=0 Radius=10 StartAngle=3.14159 EndAngle=4.71239
    g10: LineSegment StartX=289.584 StartY=10.5 StartZ=0 EndX=289.584 EndY=130.558 EndZ=0
    g11: LineSegment StartX=277.421 StartY=114.663 StartZ=0 EndX=188.321 EndY=19.4633 EndZ=0
  constraints (30):
    c: Horizontal(g1)
    c: Coincident(g2,g0)
    c: PointOnObject(g2,g-2)
    c: Horizontal(g2)
    c: Coincident(g3,g2)
    c: Coincident(g3,g1)
    c: PointOnObject(g0,g2)
    c: Tangent(g1,g0) = 1.5708
    c: PointOnObject(g6,g5)
    c: Coincident(g6,g5)
    c: PointOnObject(g7,g5)
    c: Coincident(g7,g5)
    c: PointOnObject(g8,g4)
    c: Coincident(g8,g4)
    c: PointOnObject(g9,g4)
    c: Coincident(g9,g4)
    c: Vertical(g10)
    c: Tangent(g11,g6) = 1.5708
    c: Parallel(g11,g5)
    c: Tangent(g10,g9) = 1.5708
    c: Tangent(g10,g8) = 1.5708
    c: Tangent(g11,g7) = 1.5708
    c: Distance(g6,g5) = 10
    c: Distance(g8,g4) = 10
    c: Coincident(g1,g-1)
    c: Coincident(g0,g-7)
    c: Coincident(g5,g-3)
    c: Coincident(g5,g-4)
    c: Coincident(g-5,g4)
    c: Coincident(g4,g-6)
FEATURE [PartDesign::Pocket] Pocket004
  BaseFeature = -> Bend
  Direction = (0,0,-1)
  Length = 5
  Length2 = 5
  Profile = -> Sketch017
  ReferenceAxis = -> Sketch017 [N_Axis]
  Reversed = true
  Type = 0
FEATURE [PartDesign::Pad] Pad003
  BaseFeature = -> Pocket004
  Direction = (0,0,1)
  Length = 0.3
  Length2 = 10
  Profile = -> Sketch019
  ReferenceAxis = -> Sketch019 [N_Axis]
  Type = 0
FEATURE [PartDesign::Mirrored] Mirrored
  BaseFeature = -> Pad003
  MirrorPlane = -> YZ_Plane
  Originals = -> [Pocket004,Pad003]
  Refine = true
FEATURE [Part::Part2DObjectPython] Placment007  # Draft 2D object (typed FeaturePython)
  AttacherType = Attacher::AttachEngine3D
  AttachmentOffset = pos=(0,105,0) rot=(0,1,0;4.71239rad)
  ExposePlacement = true
  MapMode = 7
  MarkerShape = 1
  MarkerSize = 20
  NumElements = 1
  Placement = pos=(164.614,9.5,105) rot=(-0.293211,0.676028,0.676028;3.71203rad)
  Support = -> [Binder]
  Type = lattice2AttachablePlacement.AttachablePlacement
  isLattice = 1
FEATURE [Sketcher::SketchObject] Sketch033
  ExternalGeometry = -> [Binder011,Sketch007]
  FullyConstrained = true
  MapMode = 2
  Placement = pos=(164.614,9.5,105) rot=(-0.293211,0.676028,0.676028;3.71203rad)
  Support = -> [Placment007]
  sketch-geometry (7):
    g0: LineSegment StartX=-150.565 StartY=0 StartZ=0 EndX=-150.565 EndY=11.5539 EndZ=0
    g1: LineSegment StartX=-150.565 StartY=11.5539 StartZ=0 EndX=-17.8174 EndY=1.36726 EndZ=0
    g2: LineSegment StartX=0.05 StartY=0 StartZ=0 EndX=-150.565 EndY=0 EndZ=0
    g3: ArcOfCircle CenterX=-1 CenterY=0 CenterZ=0 NormalX=0 NormalY=0 NormalZ=1 AngleXU=0 Radius=15 StartAngle=1.5708 EndAngle=2.94255
    g4: ArcOfCircle CenterX=-17.6644 CenterY=3.3614 CenterZ=0 NormalX=0 NormalY=0 NormalZ=1 AngleXU=0 Radius=2 StartAngle=4.6358 EndAngle=6.08414
    g5: LineSegment StartX=-1 StartY=15 StartZ=0 EndX=0.05 EndY=15 EndZ=0
    g6: LineSegment StartX=0.05 StartY=0 StartZ=0 EndX=0.05 EndY=15 EndZ=0
  constraints (20):
    c: PointOnObject(g0,g-1)
    c: PointOnObject(g0,g-3)
    c: Vertical(g0)
    c: Coincident(g0,g1)
    c: Coincident(g2,g0)
    c: Vertical(g-4,g0)
    c: PointOnObject(g3,g-1)
    c: Tangent(g4,g3) = 1.5708
    c: Tangent(g1,g4) = -1.5708
    c: Tangent(g5,g3) = 1.5708
    c: Horizontal(g5)
    c: Radius(g3) = 15
    c: PointOnObject(g1,g-3)
    c: DistanceX(g3) = -1
    c: Radius(g4) = 2
    c: Coincident(g2,g6)
    c: PointOnObject(g-3,g2)
    c: Vertical(g6)
    c: Coincident(g5,g6)
    c: DistanceX(g5) = 0.05
FEATURE [Part::FeaturePython] Mirror014  label="Mirror014 of Placment007"  # WARN: FeaturePython — macro-defined, semantics opaque (R4)
  ExposePlacement = false
  FlipX = true
  FlipY = false
  FlipZ = false
  MarkerShape = 1
  MarkerSize = 20
  NumElements = 1
  Object = -> Placment007
  ObjectTraversal = 0
  Type = lattice2Mirror.LatticeMirror
  isLattice = 1
FEATURE [Sketcher::SketchObject] Sketch034
  ExternalGeometry = -> [Binder011,Sketch007]
  FullyConstrained = true
  MapMode = 6
  Placement = pos=(-164.614,9.5,105) rot=(0.293211,0.676028,0.676028;2.57116rad)
  Support = -> [Mirror014]
  sketch-geometry (7):
    g0: LineSegment StartX=17.8108 StartY=2.44068 StartZ=0 EndX=150.565 EndY=13.1789 EndZ=0
    g1: LineSegment StartX=150.565 StartY=13.1789 StartZ=0 EndX=150.565 EndY=0 EndZ=0
    g2: LineSegment StartX=150.565 StartY=0 StartZ=0 EndX=-0.05 EndY=0 EndZ=0
    g3: LineSegment StartX=-0.05 StartY=0 StartZ=0 EndX=-0.05 EndY=16 EndZ=0
    g4: LineSegment StartX=-0.05 StartY=16 StartZ=0 EndX=1 EndY=16 EndZ=0
    g5: ArcOfCircle CenterX=1 CenterY=1 CenterZ=0 NormalX=0 NormalY=0 NormalZ=1 AngleXU=0 Radius=15 StartAngle=0.20341 EndAngle=1.5708
    g6: ArcOfCircle CenterX=17.6495 CenterY=4.43417 CenterZ=0 NormalX=0 NormalY=0 NormalZ=1 AngleXU=0 Radius=2 StartAngle=3.345 EndAngle=4.7931
  constraints (20):
    c: PointOnObject(g0,g-3)
    c: PointOnObject(g0,g-3)
    c: Coincident(g0,g1)
    c: PointOnObject(g1,g-1)
    c: Vertical(g1)
    c: Coincident(g1,g2)
    c: Coincident(g3,g4)
    c: Horizontal(g4)
    c: Tangent(g6,g0) = -1.5708
    c: Tangent(g6,g5) = 1.5708
    c: Horizontal(g5,g-3)
    c: Radius(g5) = 15
    c: Tangent(g5,g4) = 1.5708
    c: Radius(g6) = 2
    c: Vertical(g-4,g1)
    c: DistanceX(g4) = 1
    c: Coincident(g2,g3)
    c: PointOnObject(g2,g-1)
    c: Vertical(g3)
    c: DistanceX(g2) = -0.05
FEATURE [Sketcher::SketchObject] Sketch035
  ExternalGeometry = -> [Binder011]
  FullyConstrained = true
  MapMode = 5
  Placement = pos=(0,0,0) rot=(1,0,0;1.5708rad)
  Support = -> [XZ_Plane]
  sketch-geometry (10):
    g0: LineSegment StartX=-164.414 StartY=121 StartZ=0 EndX=-165.414 EndY=121 EndZ=0
    g1: LineSegment StartX=-165.414 StartY=121 StartZ=0 EndX=-165.414 EndY=105 EndZ=0
    g2: LineSegment StartX=-165.414 StartY=105 StartZ=0 EndX=165.414 EndY=105 EndZ=0
    g3: LineSegment StartX=165.414 StartY=105 StartZ=0 EndX=165.414 EndY=120 EndZ=0
    g4: LineSegment StartX=165.414 StartY=120 StartZ=0 EndX=164.414 EndY=120 EndZ=0
    g5: ArcOfCircle CenterX=-147.526 CenterY=107.948 CenterZ=0 NormalX=0 NormalY=0 NormalZ=1 AngleXU=0 Radius=2 StartAngle=3.25644 EndAngle=4.70935
    g6: ArcOfCircle CenterX=147.538 CenterY=107.052 CenterZ=0 NormalX=0 NormalY=0 NormalZ=1 AngleXU=0 Radius=2 StartAngle=4.70935 EndAngle=6.16219
    g7: LineSegment StartX=147.532 StartY=105.052 StartZ=0 EndX=-147.532 EndY=105.948 EndZ=0
    g8: ArcOfCircle CenterX=-164.414 CenterY=106 CenterZ=0 NormalX=0 NormalY=0 NormalZ=1 AngleXU=0 Radius=15 StartAngle=0.114847 EndAngle=1.5708
    g9: ArcOfCircle CenterX=164.414 CenterY=105 CenterZ=0 NormalX=0 NormalY=0 NormalZ=1 AngleXU=0 Radius=15 StartAngle=1.5708 EndAngle=3.0206
  constraints (28):
    c: Horizontal(g0)
    c: Coincident(g0,g1)
    c: Coincident(g1,g2)
    c: Horizontal(g2)
    c: Coincident(g2,g3)
    c: Vertical(g3)
    c: Coincident(g3,g4)
    c: Horizontal(g4)
    c: PointOnObject(g-3,g2)
    c: Coincident(g7,g6)
    c: Tangent(g6,g-3) = 1.5708
    c: Tangent(g7,g5) = 1.5708
    c: PointOnObject(g5,g-3)
    c: Equal(g5,g6)
    c: Radius(g5) = 2
    c: DistanceX(g-3,g0) = 0.2
    c: DistanceX(g4,g-3) = 0.2
    c: DistanceX(g0,g0) = 1
    c: Vertical(g1)
    c: Horizontal(g8,g-3)
    c: Tangent(g8,g0) = -1.5708
    c: Tangent(g8,g5) = 1.5708
    c: Equal(g4,g0)
    c: Tangent(g9,g4) = -1.5708
    c: Horizontal(g9,g-3)
    c: Tangent(g9,g6) = 1.5708
    c: Equal(g9,g8)
    c: Radius(g8) = 15
FEATURE [PartDesign::SubShapeBinder] Binder031
  BindCopyOnChange = 0
  BindMode = 0
  ClaimChildren = false
  Context = -> Body [Binder031.]
  Fuse = false
  MakeFace = false
  OffsetFill = false
  OffsetIntersection = false
  OffsetJoinType = 0
  OffsetOpenResult = false
  PartialLoad = false
  Relative = true
  Support = -> [Sketch049]
  _Version = 2
FEATURE [PartDesign::Pocket] Pocket002
  BaseFeature = -> Mirrored
  Direction = (0,0,-1)
  Length = 105
  Length2 = 5
  Profile = -> Binder031
  Reversed = true
  Type = 0
FEATURE [PartDesign::Pocket] Pocket007
  BaseFeature = -> Pocket002
  Direction = (0.730107,-0.683333,-2e-16)
  Length = 0.3
  Length2 = 5
  Profile = -> Sketch033
  ReferenceAxis = -> Sketch033 [N_Axis]
  Type = 4
FEATURE [PartDesign::Pocket] Pocket008
  BaseFeature = -> Pocket007
  Direction = (-0.730107,-0.683333,1e-16)
  Length = 0.3
  Length2 = 5
  Profile = -> Sketch034
  ReferenceAxis = -> Sketch034 [N_Axis]
  Type = 4
FEATURE [PartDesign::Pocket] Pocket009
  BaseFeature = -> Pocket008
  Direction = (0,1,-2e-16)
  Length = 9.5
  Length2 = 5
  Profile = -> Sketch035
  ReferenceAxis = -> Sketch035 [N_Axis]
  Refine = true
  Type = 0
  expr: Length = <<face_main_sketch>>.Constraints.offset
FEATURE [PartDesign::Boolean] Boolean007
  BaseFeature = -> Pocket009
  Group = -> [BaseBend002,BaseBend003]
  Type = 0
FEATURE [PartDesign::Boolean] Boolean  label="face2_origin"
  BaseFeature = -> Boolean007
  Group = -> [Compound002]
  Type = 1
FEATURE [PartDesign::Boolean] Boolean003
  BaseFeature = -> Boolean
  Group = -> [Compound012]
  Type = 1
FEATURE [PartDesign::Body] Body  label="face_material_0.30ansi"
  Group = -> [Binder002,Binder,BaseBend,Sketch009,Local_CS,Extend,Bend,Binder006,Sketch017,Sketch019,Binder021,Pocket004,Pad003,Mirrored,Binder031,Pocket002,Placment007,Sketch033,Sketch034,Sketch035,Pocket007,Pocket008,Pocket009,Boolean007,Boolean,Sketch007,Binder011,Boolean003,Mirror014]
  Origin = -> Origin
  Tip = -> Mirrored
COMPONENT P23 — recipe-attached ("bottom", modeled in this document).
Construction recipe (the document's own serialized feature program — sketch geometry with constraints, then the solid features built on it; lengths are millimeters unless a unit is written):

FEATURE [PartDesign::SubShapeBinder] Binder014
  BindCopyOnChange = 0
  BindMode = 0
  ClaimChildren = true
  Context = -> Body006 [Binder014.]
  Fuse = false
  MakeFace = true
  OffsetFill = false
  OffsetIntersection = false
  OffsetJoinType = 0
  OffsetOpenResult = false
  PartialLoad = false
  Relative = false
  Support = -> [Populate019]
  _Version = 2
FEATURE [PartDesign::Pad] Pad004
  Direction = (0,0,1)
  Length = 3
  Length2 = 10
  Profile = -> Binder014
  Type = 0
FEATURE [PartDesign::SubShapeBinder] Binder015
  BindCopyOnChange = 0
  BindMode = 0
  ClaimChildren = true
  Context = -> Body011 [Binder015.]
  Fuse = false
  MakeFace = true
  OffsetFill = false
  OffsetIntersection = false
  OffsetJoinType = 0
  OffsetOpenResult = false
  PartialLoad = false
  Relative = false
  Support = -> [Populate019]
  _Version = 2
FEATURE [PartDesign::Pad] Pad005
  Direction = (0,0,1)
  Length = 0.3
  Length2 = 10
  Profile = -> Binder015
  Reversed = true
  Type = 0
FEATURE [PartDesign::FeaturePython] Bend002  # WARN: FeaturePython — macro-defined, semantics opaque (R4)
  AutoMiter = true
  BaseFeature = -> Pad005
  BendType = 1
  LengthList = [3]
  LengthSpec = 1
  ReliefFactor = 0.7
  UseReliefFactor = false
  angle = 90
  baseObject = -> Pad005 [Edge33,Edge59]
  bendAList = [90]
  extend1 = 0
  extend2 = 0
  gap1 = 0
  gap2 = 0
  invert = false
  kfactor = 0.5
  length = 3
  maxExtendDist = 5
  minGap = 0.1
  minReliefGap = 1
  miterangle1 = 0
  miterangle2 = 0
  offset = 0
  radius = 0.1
  reliefType = 0
  reliefd = 1
  reliefw = 0.8
  sketchflip = false
  sketchinvert = false
  unfold = false
FEATURE [PartDesign::Boolean] Boolean011
  BaseFeature = -> Pad004
  Group = -> [Compound019]
  Refine = true
  Type = 1
FEATURE [PartDesign::Body] Body006  label="bottomPP"
  Group = -> [Binder014,Pad004,Boolean011]
  Origin = -> Origin007
  Placement = pos=(0,0,-3) rot=(0,0,1;0rad)
  Tip = -> Boolean011
FEATURE [PartDesign::Boolean] Boolean012
  BaseFeature = -> Bend002
  Group = -> [Compound020]
  Type = 1
FEATURE [PartDesign::Body] Body011  label="bottom_composit_material_0.30ansi"
  Group = -> [Binder015,Pad005,Bend002,Boolean012]
  Origin = -> Origin012
  Placement = pos=(0,0,-3) rot=(0,0,1;0rad)
  Tip = -> Boolean012
COMPONENT P24 — geometry summary ("cap"; no construction recipe available for this part):
  bounding box: 600.2 x 351.5 x 70.4 mm
  tessellated surface: 7,892 triangles
  volume: 177350 mm^3 (1% of its bounding box)
  symmetry: mirror-symmetric across its y mid-plane
PROVENANCE & LICENSES
A FreeCAD (.FCStd) document from a public repository crawl; recipes are the document's own serialized feature recipes (and, for linked parts, companion documents' recipes).
License: as declared in the source repository (recorded in the dataset sidecar).
